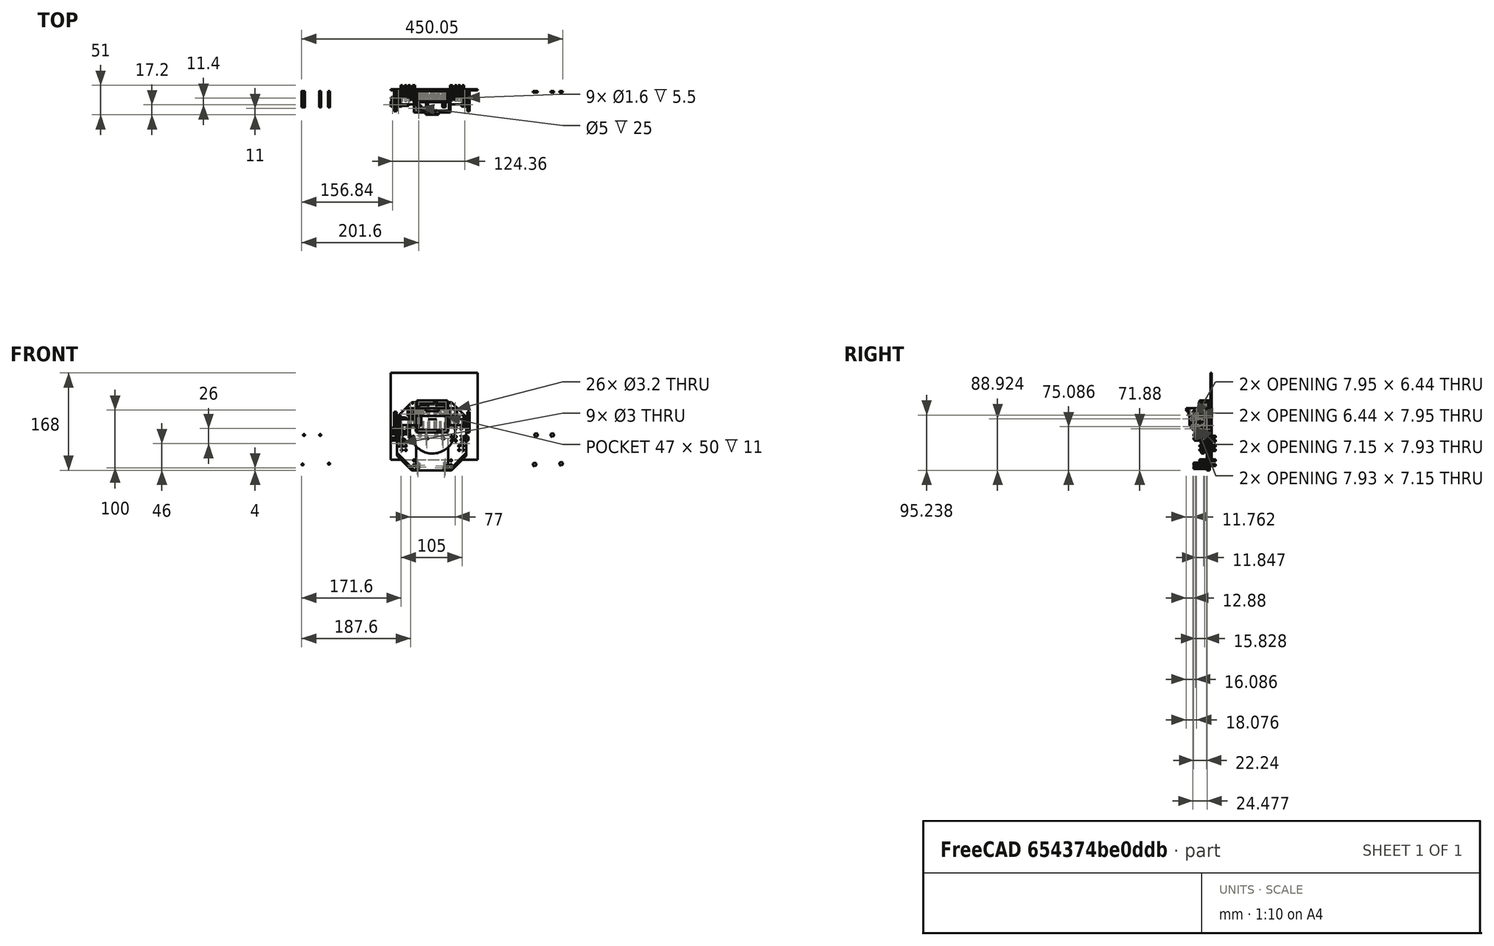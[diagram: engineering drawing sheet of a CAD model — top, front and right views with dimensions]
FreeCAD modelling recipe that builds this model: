
FCSTD DOCUMENT  (FreeCAD 0.17R13522 (Git))
Label: 5028.7 Frank
License: All rights reserved
LicenseURL: http://en.wikipedia.org/wiki/All_rights_reserved
objects: Part::Cylinder×138, Part::Box×78, Part::Cut×74, Part::Fuse×72, Part::MultiFuse×39, Part::Feature×37, Part::Chamfer×23, Part::Fillet×19, Part::Mirroring×15, Part::Cone×9, Part::Compound×3, Part::Torus×2, App::DocumentObjectGroup×1
note: 509 computed .brp shape members not serialized (recipe doc carries the construction recipe); baked Part::Feature solids carry a one-line shape summary decoded from their .brp

FEATURE [Part::Cylinder] Cylinder
  Angle = 360
  AttacherType = Attacher::AttachEngine3D
  Height = 30
  Radius = 7
FEATURE [Part::Cylinder] Cylinder001
  Angle = 360
  AttacherType = Attacher::AttachEngine3D
  Height = 19
  Placement = pos=(0,0,30) rot=(0,0,1;0rad)
  Radius = 7
FEATURE [Part::Cylinder] Cylinder002
  Angle = 360
  AttacherType = Attacher::AttachEngine3D
  Height = 1.8
  Placement = pos=(0,0,49) rot=(0,0,1;0rad)
  Radius = 2.5
FEATURE [Part::Compound] Compound
  Links = -> [Cylinder,Cylinder002,Cylinder001]
FEATURE [Part::Cylinder] Cylinder003
  Angle = 360
  AttacherType = Attacher::AttachEngine3D
  Height = 30
  Radius = 7
FEATURE [Part::Cylinder] Cylinder004
  Angle = 360
  AttacherType = Attacher::AttachEngine3D
  Height = 19
  Placement = pos=(0,0,30) rot=(0,0,1;0rad)
  Radius = 7
FEATURE [Part::Cylinder] Cylinder005
  Angle = 360
  AttacherType = Attacher::AttachEngine3D
  Height = 1.8
  Placement = pos=(0,0,49) rot=(0,0,1;0rad)
  Radius = 2.5
FEATURE [Part::Compound] Compound001
  Links = -> [Cylinder003,Cylinder005,Cylinder004]
  Placement = pos=(14.5,0,50) rot=(1,0,0;3.14159rad)
FEATURE [Part::Cylinder] Cylinder006
  Angle = 360
  AttacherType = Attacher::AttachEngine3D
  Height = 30
  Radius = 7
FEATURE [Part::Cylinder] Cylinder007
  Angle = 360
  AttacherType = Attacher::AttachEngine3D
  Height = 19
  Placement = pos=(0,0,30) rot=(0,0,1;0rad)
  Radius = 7
FEATURE [Part::Cylinder] Cylinder008
  Angle = 360
  AttacherType = Attacher::AttachEngine3D
  Height = 1.8
  Placement = pos=(0,0,49) rot=(0,0,1;0rad)
  Radius = 2.5
FEATURE [Part::Compound] Compound002
  Links = -> [Cylinder006,Cylinder008,Cylinder007]
  Placement = pos=(29,0,0) rot=(0,0,1;0rad)
FEATURE [Part::Box] Box  label="Cube"
  AttacherType = Attacher::AttachEngine3D
  Height = 50
  Length = 47
  Placement = pos=(-9,-8,0) rot=(0,0,1;0rad)
  Width = 12
FEATURE [Part::Box] Box001  label="Cube001"
  AttacherType = Attacher::AttachEngine3D
  Height = 55
  Length = 53
  Placement = pos=(-12,-8,-2.5) rot=(0,0,1;0rad)
  Width = 11
FEATURE [Part::Cylinder] Cylinder009
  Angle = 360
  AttacherType = Attacher::AttachEngine3D
  Height = 50
  Radius = 7
FEATURE [Part::Cylinder] Cylinder010
  Angle = 360
  AttacherType = Attacher::AttachEngine3D
  Height = 50
  Placement = pos=(14.5,0,0) rot=(0,0,1;0rad)
  Radius = 7
FEATURE [Part::Cut] Cut
  Base = -> Box001
  Tool = -> Box
FEATURE [Part::Box] Box002  label="Cube002"
  AttacherType = Attacher::AttachEngine3D
  Height = 55
  Length = 53
  Placement = pos=(-12,3,-2.5) rot=(0,0,1;0rad)
  Width = 7
FEATURE [Part::Fuse] Fusion
  Base = -> Cut
  Tool = -> Box002
FEATURE [Part::Cut] Cut001  label="No idea why this is here...."
  Base = -> Fusion
  Tool = -> Cylinder009
FEATURE [Part::Cylinder] Cylinder011
  Angle = 360
  AttacherType = Attacher::AttachEngine3D
  Height = 50
  Placement = pos=(29,0,0) rot=(0,0,1;0rad)
  Radius = 7
FEATURE [Part::Box] Box003  label="Cube003"
  AttacherType = Attacher::AttachEngine3D
  Height = 5
  Length = 2
  Placement = pos=(28,-9,-2) rot=(0,0,1;0rad)
  Width = 12
FEATURE [Part::Box] Box004  label="Cube004"
  AttacherType = Attacher::AttachEngine3D
  Height = 5
  Length = 2
  Placement = pos=(18.5,-9,46) rot=(0,0,1;0rad)
  Width = 12
FEATURE [Part::Box] Box005  label="Cube005"
  AttacherType = Attacher::AttachEngine3D
  Height = 5
  Length = 2
  Placement = pos=(-2,-9,46) rot=(0,0,1;0rad)
  Width = 12
FEATURE [Part::Box] Box006  label="Cube006"
  AttacherType = Attacher::AttachEngine3D
  Height = 5
  Length = 3
  Placement = pos=(35,-9,-4) rot=(0,0,1;0rad)
  Width = 12
FEATURE [Part::Cut] Cut008
FEATURE [Part::Torus] Torus001
  Angle1 = -180
  Angle2 = 180
  Angle3 = 360
  AttacherType = Attacher::AttachEngine3D
  Placement = pos=(0,0,2) rot=(0,0,1;0rad)
  Radius1 = 19
  Radius2 = 1.5
FEATURE [Part::Cut] Cut009  label="wheel2"
  Base = -> Cut008
  Placement = pos=(75,-7,15) rot=(0,1,0;1.5708rad)
  Tool = -> Torus001
FEATURE [Part::Torus] Torus
  Angle1 = -180
  Angle2 = 180
  Angle3 = 360
  AttacherType = Attacher::AttachEngine3D
  Placement = pos=(0,0,2) rot=(0,0,1;0rad)
  Radius1 = 19
  Radius2 = 1.5
FEATURE [Part::Cut] Cut010
FEATURE [Part::Cut] Cut011  label="wheel1"
  Base = -> Cut010
  Placement = pos=(-51,-7,15) rot=(0,1,0;1.5708rad)
  Tool = -> Torus
FEATURE [Part::Fuse] Fusion003
FEATURE [Part::Cylinder] Cylinder012
  Angle = 360
  AttacherType = Attacher::AttachEngine3D
  Height = 10
  Placement = pos=(5,-4.5,0) rot=(0,1,0;1.5708rad)
  Radius = 0.8
FEATURE [Part::Fuse] Fusion048  label="right-motor001"
  Base = -> Cylinder012
  Placement = pos=(-51,-7,15) rot=(0,0,1;0rad)
  Tool = -> Fusion003
FEATURE [Part::Fuse] Fusion049
FEATURE [Part::Cylinder] Cylinder013
  Angle = 360
  AttacherType = Attacher::AttachEngine3D
  Height = 10
  Placement = pos=(5,-4.5,0) rot=(0,1,0;1.5708rad)
  Radius = 0.8
FEATURE [Part::Fuse] Fusion050  label="left-motor001"
  Base = -> Cylinder013
  Placement = pos=(79,-7,15) rot=(0,0,1;3.14159rad)
  Tool = -> Fusion049
FEATURE [Part::Box] Box007  label="Cube007"
  AttacherType = Attacher::AttachEngine3D
  Height = 5
  Length = 2
  Placement = pos=(37.5,-9,46) rot=(0,0,1;0rad)
  Width = 12
FEATURE [Part::Box] Box008  label="Cube008"
  AttacherType = Attacher::AttachEngine3D
  Height = 5
  Length = 2
  Placement = pos=(8,-9,-2) rot=(0,0,1;0rad)
  Width = 12
FEATURE [Part::Box] Box009  label="The Ground"
  AttacherType = Attacher::AttachEngine3D
  Height = 150
  Length = 150
  Placement = pos=(-57,11,-50) rot=(0,0,1;0rad)
  Width = 2
FEATURE [Part::Box] Box010  label="Motor Mount Left"
  AttacherType = Attacher::AttachEngine3D
  Height = 16
  Length = 4
  Placement = pos=(69,-13,7) rot=(0,0,1;0rad)
  Width = 20
FEATURE [Part::Box] Box011  label="Motor Mount Right"
  AttacherType = Attacher::AttachEngine3D
  Height = 16
  Length = 4
  Placement = pos=(-46,-13,7) rot=(0,0,1;0rad)
  Width = 20
FEATURE [Part::Box] Box012  label="Motor Support Right"
  AttacherType = Attacher::AttachEngine3D
  Height = 16
  Length = 10
  Placement = pos=(-25,-1,7) rot=(0,0,1;0rad)
  Width = 8
FEATURE [Part::Box] Box013  label="Motor Support Left"
  AttacherType = Attacher::AttachEngine3D
  Height = 16
  Length = 10
  Placement = pos=(43,-1,7) rot=(0,0,1;0rad)
  Width = 8
FEATURE [Part::Cylinder] Cylinder014
  Angle = 360
  AttacherType = Attacher::AttachEngine3D
  Height = 28
  Placement = pos=(40.7,0,-10.3) rot=(1,0,0;1.5708rad)
  Radius = 1.6
FEATURE [Part::Cylinder] Cylinder015
  Angle = 360
  AttacherType = Attacher::AttachEngine3D
  Height = 28
  Placement = pos=(-2.4,0,-59.8) rot=(1,0,0;1.5708rad)
  Radius = 1.6
FEATURE [Part::Cylinder] Cylinder016
  Angle = 360
  AttacherType = Attacher::AttachEngine3D
  Height = 28
  Placement = pos=(-5,0,-9) rot=(1,0,0;1.5708rad)
  Radius = 1.6
FEATURE [Part::Cylinder] Cylinder017
  Angle = 360
  AttacherType = Attacher::AttachEngine3D
  Height = 28
  Placement = pos=(25.5,0,-59.8) rot=(1,0,0;1.5708rad)
  Radius = 1.6
FEATURE [Part::Fuse] Fusion051
  Base = -> Cylinder015
  Tool = -> Cylinder016
FEATURE [Part::Fuse] Fusion052
  Base = -> Cylinder014
  Tool = -> Cylinder017
FEATURE [Part::Fuse] Fusion053  label="Screw holes on Arduino Duo"
  Base = -> Fusion051
  Tool = -> Fusion052
FEATURE [Part::Mirroring] Part__Mirroring  label="XXXXXScrew holes on Arduino Duo (Mirror #1)"
  Base = (0,0,0)
  Normal = (0,0,1)
  Placement = pos=(-204,10,-67) rot=(0,0,1;0rad)
  Source = -> Fusion053
FEATURE [Part::Box] Box014  label="Not used Cube"
  AttacherType = Attacher::AttachEngine3D
  Height = 10
  Length = 10
  Placement = pos=(-1,4,-5.85) rot=(0,0,1;0rad)
  Width = 10
FEATURE [Part::Box] Box015  label="Cube014 Arduino Support cube"
  AttacherType = Attacher::AttachEngine3D
  Height = 67
  Length = 55
  Placement = pos=(-13,5,-68) rot=(0,0,1;0rad)
  Width = 5
FEATURE [Part::Cylinder] Cylinder018
  Angle = 360
  AttacherType = Attacher::AttachEngine3D
  Height = 5
  Placement = pos=(15,0,0) rot=(1,0,0;1.5708rad)
  Radius = 39
FEATURE [Part::Cut] Cut014  label="M3 Nut"
  Base = -> Cut001
  Placement = pos=(-6.4,10,-7.2) rot=(1,0,0;1.5708rad)
  Tool = -> Cylinder001
FEATURE [Part::Cut] Cut015  label="M3 Nut001"
  Base = -> Cut001
  Placement = pos=(21.5,10,-7.2) rot=(1,0,0;1.5708rad)
  Tool = -> Cylinder001
FEATURE [Part::Cut] Cut016  label="M3 Nut002"
  Base = -> Cut001
  Placement = pos=(36.7,10,-56.7) rot=(1,0,0;1.5708rad)
  Tool = -> Cylinder001
FEATURE [Part::Cut] Cut017  label="M3 Nut003"
  Base = -> Cut001
  Placement = pos=(-9,10,-58) rot=(1,0,0;1.5708rad)
  Tool = -> Cylinder001
FEATURE [Part::Cut] Cut018
  Base = -> Cut
  Placement = pos=(-9,10,-58) rot=(1,0,0;1.5708rad)
  Tool = -> Box006
FEATURE [Part::Cut] Cut019
  Base = -> Cut
  Placement = pos=(36.7,10,-56.7) rot=(1,0,0;1.5708rad)
  Tool = -> Box006
FEATURE [Part::Cut] Cut020
  Base = -> Cut
  Placement = pos=(-6.4,10,-7.2) rot=(1,0,0;1.5708rad)
  Tool = -> Box006
FEATURE [Part::Cut] Cut021
  Base = -> Cut
  Placement = pos=(21.5,10,-7.2) rot=(1,0,0;1.5708rad)
  Tool = -> Box006
FEATURE [Part::MultiFuse] Fusion054  label="XXXXXHex Holes"
  Placement = pos=(200,0,0) rot=(0,0,1;0rad)
  Shapes = -> [Cut018,Cut021,Cut019,Cut020]
FEATURE [Part::Box] Box016  label="Cube015"
  AttacherType = Attacher::AttachEngine3D
  Height = 117
  Length = 33
  Placement = pos=(-46,7,-68) rot=(0,0,1;0rad)
  Width = 3
FEATURE [Part::Box] Box017  label="Cube016"
  AttacherType = Attacher::AttachEngine3D
  Height = 117
  Length = 31
  Placement = pos=(42,7,-68) rot=(0,0,1;0rad)
  Width = 3
FEATURE [Part::Cylinder] Cylinder019
  Angle = 360
  AttacherType = Attacher::AttachEngine3D
  Height = 28
  Placement = pos=(48,20,-10) rot=(1,0,0;1.5708rad)
  Radius = 1.6
FEATURE [Part::Cylinder] Cylinder020
  Angle = 360
  AttacherType = Attacher::AttachEngine3D
  Height = 28
  Placement = pos=(47,20,-51) rot=(1,0,0;1.5708rad)
  Radius = 1.6
FEATURE [Part::Cylinder] Cylinder021
  Angle = 360
  AttacherType = Attacher::AttachEngine3D
  Height = 28
  Placement = pos=(48,20,-17) rot=(1,0,0;1.5708rad)
  Radius = 1.6
FEATURE [Part::Cylinder] Cylinder022
  Angle = 360
  AttacherType = Attacher::AttachEngine3D
  Height = 28
  Placement = pos=(47,20,-59) rot=(1,0,0;1.5708rad)
  Radius = 1.6
FEATURE [Part::Cylinder] Cylinder023
  Angle = 360
  AttacherType = Attacher::AttachEngine3D
  Height = 28
  Placement = pos=(55,20,-17) rot=(1,0,0;1.5708rad)
  Radius = 1.6
FEATURE [Part::Cylinder] Cylinder024
  Angle = 360
  AttacherType = Attacher::AttachEngine3D
  Height = 28
  Placement = pos=(55,20,-10) rot=(1,0,0;1.5708rad)
  Radius = 1.6
FEATURE [Part::MultiFuse] Fusion055
  Shapes = -> [Cylinder021,Cylinder023,Cylinder024,Cylinder019]
FEATURE [Part::MultiFuse] Fusion056
  Placement = pos=(13,0,-16) rot=(0,0,1;0rad)
  Shapes = -> [Cylinder021,Cylinder023,Cylinder024,Cylinder019]
FEATURE [Part::MultiFuse] Fusion057  label="Mount holes top left"
  Placement = pos=(-1,0,46) rot=(0,0,1;0rad)
  Shapes = -> [Cylinder021,Cylinder023,Cylinder024,Cylinder019]
FEATURE [Part::MultiFuse] Fusion058  label="Mount holes top right"
  Placement = pos=(-71,0,46) rot=(0,0,1;0rad)
  Shapes = -> [Cylinder021,Cylinder023,Cylinder024,Cylinder019]
FEATURE [Part::MultiFuse] Fusion059
  Shapes = -> [Cylinder022,Cylinder020,Fusion055,Fusion056]
FEATURE [Part::Mirroring] Part__Mirroring001  label="Mount holes bottom right"
  Base = (0,0,0)
  Normal = (1,0,0)
  Placement = pos=(30,0,0) rot=(0,0,1;0rad)
  Source = -> Fusion059
FEATURE [Part::Cylinder] Cylinder025
  Angle = 360
  AttacherType = Attacher::AttachEngine3D
  Height = 28
  Placement = pos=(48,20,-10) rot=(1,0,0;1.5708rad)
  Radius = 1.6
FEATURE [Part::Cylinder] Cylinder026
  Angle = 360
  AttacherType = Attacher::AttachEngine3D
  Height = 28
  Placement = pos=(47,20,-51) rot=(1,0,0;1.5708rad)
  Radius = 1.6
FEATURE [Part::Cylinder] Cylinder027
  Angle = 360
  AttacherType = Attacher::AttachEngine3D
  Height = 28
  Placement = pos=(48,20,-17) rot=(1,0,0;1.5708rad)
  Radius = 1.6
FEATURE [Part::Cylinder] Cylinder028
  Angle = 360
  AttacherType = Attacher::AttachEngine3D
  Height = 28
  Placement = pos=(47,20,-59) rot=(1,0,0;1.5708rad)
  Radius = 1.6
FEATURE [Part::Cylinder] Cylinder029
  Angle = 360
  AttacherType = Attacher::AttachEngine3D
  Height = 28
  Placement = pos=(55,20,-17) rot=(1,0,0;1.5708rad)
  Radius = 1.6
FEATURE [Part::Cylinder] Cylinder030
  Angle = 360
  AttacherType = Attacher::AttachEngine3D
  Height = 28
  Placement = pos=(55,20,-10) rot=(1,0,0;1.5708rad)
  Radius = 1.6
FEATURE [Part::MultiFuse] Fusion060
  Shapes = -> [Cylinder027,Cylinder029,Cylinder030,Cylinder025]
FEATURE [Part::MultiFuse] Fusion061
  Placement = pos=(13,0,-16) rot=(0,0,1;0rad)
  Shapes = -> [Cylinder027,Cylinder029,Cylinder030,Cylinder025]
FEATURE [Part::MultiFuse] Fusion062  label="Mount holes bottom left"
  Shapes = -> [Cylinder028,Cylinder026,Fusion060,Fusion061]
FEATURE [Part::Cylinder] Cylinder031  label="Cylinder127"
  Angle = 360
  AttacherType = Attacher::AttachEngine3D
  Height = 10
  Placement = pos=(0,18,29) rot=(0,0,1;0rad)
  Radius = 2.25
FEATURE [Part::Cylinder] Cylinder032  label="Cylinder128"
  Angle = 360
  AttacherType = Attacher::AttachEngine3D
  Height = 10
  Placement = pos=(4.5,18,32) rot=(0,0,1;0rad)
  Radius = 1
FEATURE [Part::Cylinder] Cylinder033  label="Cylinder129"
  Angle = 360
  AttacherType = Attacher::AttachEngine3D
  Height = 10
  Placement = pos=(-4.5,18,32) rot=(0,0,1;0rad)
  Radius = 1
FEATURE [Part::Fuse] Fusion009  label="Mounting Screw Holes"
  Base = -> Cylinder032
  Tool = -> Cylinder033
FEATURE [Part::Fuse] Fusion071  label="Motor Holes Left"
  Base = -> Cylinder031
  Placement = pos=(37,-7,-3) rot=(0.57735,0.57735,0.57735;2.0944rad)
  Tool = -> Fusion009
FEATURE [Part::Cylinder] Cylinder034  label="Cylinder130"
  Angle = 360
  AttacherType = Attacher::AttachEngine3D
  Height = 10
  Placement = pos=(0,18,29) rot=(0,0,1;0rad)
  Radius = 2.25
FEATURE [Part::Cylinder] Cylinder035  label="Cylinder131"
  Angle = 360
  AttacherType = Attacher::AttachEngine3D
  Height = 10
  Placement = pos=(4.5,18,32) rot=(0,0,1;0rad)
  Radius = 1
FEATURE [Part::Cylinder] Cylinder036  label="Cylinder132"
  Angle = 360
  AttacherType = Attacher::AttachEngine3D
  Height = 10
  Placement = pos=(-4.5,18,32) rot=(0,0,1;0rad)
  Radius = 1
FEATURE [Part::Fuse] Fusion072  label="Mounting Screw Holes001"
  Base = -> Cylinder035
  Tool = -> Cylinder036
FEATURE [Part::Fuse] Fusion073  label="Motor Holes Right"
  Base = -> Cylinder034
  Placement = pos=(-79,-7,-3) rot=(0.57735,0.57735,0.57735;2.0944rad)
  Tool = -> Fusion072
FEATURE [Part::Cylinder] Cylinder037  label="Cylinder133"
  Angle = 360
  AttacherType = Attacher::AttachEngine3D
  Height = 28
  Placement = pos=(40.7,0,-10.3) rot=(1,0,0;1.5708rad)
  Radius = 1.6
FEATURE [Part::Cylinder] Cylinder038  label="Cylinder134"
  Angle = 360
  AttacherType = Attacher::AttachEngine3D
  Height = 28
  Placement = pos=(-2.4,0,-59.8) rot=(1,0,0;1.5708rad)
  Radius = 1.6
FEATURE [Part::Cylinder] Cylinder039  label="Cylinder135"
  Angle = 360
  AttacherType = Attacher::AttachEngine3D
  Height = 28
  Placement = pos=(-5,0,-9) rot=(1,0,0;1.5708rad)
  Radius = 1.6
FEATURE [Part::Cylinder] Cylinder040  label="Cylinder136"
  Angle = 360
  AttacherType = Attacher::AttachEngine3D
  Height = 28
  Placement = pos=(25.5,0,-59.8) rot=(1,0,0;1.5708rad)
  Radius = 1.6
FEATURE [Part::Fuse] Fusion074
  Base = -> Cylinder038
  Tool = -> Cylinder039
FEATURE [Part::Fuse] Fusion075
  Base = -> Cylinder037
  Tool = -> Cylinder040
FEATURE [Part::Fuse] Fusion076  label="Screw holes on Arduino Duo001"
  Base = -> Fusion074
  Tool = -> Fusion075
FEATURE [Part::Mirroring] Part__Mirroring002  label="Screw holes on Arduino Duo (Mirror #1)001"
  Base = (0,0,0)
  Normal = (0,0,1)
  Placement = pos=(-4,10,-67) rot=(0,0,1;0rad)
  Source = -> Fusion076
FEATURE [Part::Mirroring] Part__Mirroring003  label="Screw holes on Arduino Duo (Mirror #1)001 (Mirror #4)"
  Base = (0,0,0)
  Normal = (1,0,0)
  Placement = pos=(27,0,-6) rot=(0,0,1;0rad)
  Source = -> Part__Mirroring002
FEATURE [Part::Box] Box018  label="Cube017"
  AttacherType = Attacher::AttachEngine3D
  Height = 50
  Length = 47
  Placement = pos=(-9,-8,0) rot=(0,0,1;0rad)
  Width = 12
FEATURE [Part::Box] Box019  label="Cube018"
  AttacherType = Attacher::AttachEngine3D
  Height = 55
  Length = 53
  Placement = pos=(-12,-8,-2.5) rot=(0,0,1;0rad)
  Width = 11
FEATURE [Part::Cut] Cut031
  Base = -> Box019
  Tool = -> Box018
FEATURE [Part::Box] Box020  label="Cube019"
  AttacherType = Attacher::AttachEngine3D
  Height = 5
  Length = 3
  Placement = pos=(35,-9,-4) rot=(0,0,1;0rad)
  Width = 12
FEATURE [Part::Cut] Cut032
  Base = -> Cut031
  Placement = pos=(-9,10,-58) rot=(1,0,0;1.5708rad)
  Tool = -> Box020
FEATURE [Part::Cut] Cut033
  Base = -> Cut031
  Placement = pos=(36.7,10,-56.7) rot=(1,0,0;1.5708rad)
  Tool = -> Box020
FEATURE [Part::Cut] Cut034
  Base = -> Cut031
  Placement = pos=(-6.4,10,-7.2) rot=(1,0,0;1.5708rad)
  Tool = -> Box020
FEATURE [Part::Cut] Cut035
  Base = -> Cut031
  Placement = pos=(21.5,10,-7.2) rot=(1,0,0;1.5708rad)
  Tool = -> Box020
FEATURE [Part::MultiFuse] Fusion077
  Shapes = -> [Cut032,Cut035,Cut033,Cut034]
FEATURE [Part::Mirroring] Part__Mirroring004  label="Hex Holes"
  Base = (0,0,0)
  Normal = (1,0,0)
  Placement = pos=(27,0,-6) rot=(0,0,1;0rad)
  Source = -> Fusion077
FEATURE [Part::Box] Box021  label="Cube020"
  AttacherType = Attacher::AttachEngine3D
  Height = 13
  Length = 63
  Placement = pos=(-17,-27,26) rot=(0,0,1;0rad)
  Width = 34
FEATURE [Part::Box] Box022  label="Cube021"
  AttacherType = Attacher::AttachEngine3D
  Height = 13
  Length = 12
  Placement = pos=(45,4,26) rot=(0,0,1;0rad)
  Width = 3
FEATURE [Part::Box] Box023  label="Cube022"
  AttacherType = Attacher::AttachEngine3D
  Height = 13
  Length = 12
  Placement = pos=(-28,4,26) rot=(0,0,1;0rad)
  Width = 3
FEATURE [Part::Box] Box024  label="Cube023"
  AttacherType = Attacher::AttachEngine3D
  Height = 13
  Length = 57
  Placement = pos=(-14,-24,26) rot=(0,0,1;0rad)
  Width = 31
FEATURE [Part::Cylinder] Cylinder041  label="Cylinder137"
  Angle = 360
  AttacherType = Attacher::AttachEngine3D
  Height = 28
  Placement = pos=(54,20,29) rot=(1,0,0;1.5708rad)
  Radius = 1.6
FEATURE [Part::Cylinder] Cylinder042  label="Cylinder138"
  Angle = 360
  AttacherType = Attacher::AttachEngine3D
  Height = 28
  Placement = pos=(54,20,36) rot=(1,0,0;1.5708rad)
  Radius = 1.6
FEATURE [Part::Cylinder] Cylinder043  label="Cylinder139"
  Angle = 360
  AttacherType = Attacher::AttachEngine3D
  Height = 28
  Placement = pos=(-23,20,29) rot=(1,0,0;1.5708rad)
  Radius = 1.6
FEATURE [Part::Cylinder] Cylinder044  label="Cylinder140"
  Angle = 360
  AttacherType = Attacher::AttachEngine3D
  Height = 28
  Placement = pos=(-23,20,36) rot=(1,0,0;1.5708rad)
  Radius = 1.6
FEATURE [Part::Cylinder] Cylinder045  label="Cylinder141"
  Angle = 360
  AttacherType = Attacher::AttachEngine3D
  Height = 10
  Placement = pos=(36,-17.25,32.5) rot=(0,1,0;1.5708rad)
  Radius = 2.5
FEATURE [Part::Cut] Cut037
  Base = -> Box021
  Tool = -> Box024
FEATURE [Part::Cut] Cut038
  Base = -> Cut037
  Tool = -> Cylinder045
FEATURE [Part::Box] Box025  label="Cube024"
  AttacherType = Attacher::AttachEngine3D
  Height = 5
  Length = 22
  Placement = pos=(3.5,-31,34) rot=(0,0,1;0rad)
  Width = 4
FEATURE [Part::Cylinder] Cylinder046  label="Cylinder142"
  Angle = 360
  AttacherType = Attacher::AttachEngine3D
  Height = 10
  Placement = pos=(20.75,-29,30) rot=(0,0,1;0rad)
  Radius = 0.85
FEATURE [Part::Cylinder] Cylinder047  label="Cylinder143"
  Angle = 360
  AttacherType = Attacher::AttachEngine3D
  Height = 10
  Placement = pos=(8.25,-29,40) rot=(1,0,0;3.14159rad)
  Radius = 0.85
FEATURE [Part::Fuse] Fusion078
  Base = -> Cylinder046
  Tool = -> Cylinder047
FEATURE [Part::Cut] Cut039
  Base = -> Box025
  Tool = -> Fusion078
FEATURE [Part::Fuse] Fusion079
  Base = -> Cut038
  Tool = -> Cut039
FEATURE [Part::Fuse] Fusion080
  Base = -> Cylinder043
  Tool = -> Cylinder044
FEATURE [Part::Fuse] Fusion081
  Base = -> Cylinder041
  Tool = -> Cylinder042
FEATURE [Part::Fuse] Fusion082
  Base = -> Box023
  Tool = -> Fusion079
FEATURE [Part::Fuse] Fusion083
  Base = -> Box022
  Tool = -> Fusion082
FEATURE [Part::Cut] Cut040
  Base = -> Fusion083
  Tool = -> Fusion081
FEATURE [Part::Cut] Cut041  label="Switch Bracket"
  Base = -> Cut040
  Tool = -> Fusion080
FEATURE [Part::Cylinder] Cylinder048  label="Cylinder144"
  Angle = 360
  AttacherType = Attacher::AttachEngine3D
  Height = 28
  Placement = pos=(-23,20,29) rot=(1,0,0;1.5708rad)
  Radius = 1.6
FEATURE [Part::Cylinder] Cylinder049  label="Cylinder145"
  Angle = 360
  AttacherType = Attacher::AttachEngine3D
  Height = 28
  Placement = pos=(-23,20,36) rot=(1,0,0;1.5708rad)
  Radius = 1.6
FEATURE [Part::Fuse] Fusion084
  Base = -> Cylinder048
  Placement = pos=(1,0,0) rot=(0,0,1;0rad)
  Tool = -> Cylinder049
FEATURE [Part::Cylinder] Cylinder050  label="Cylinder146"
  Angle = 360
  AttacherType = Attacher::AttachEngine3D
  Height = 28
  Placement = pos=(-23,20,29) rot=(1,0,0;1.5708rad)
  Radius = 1.6
FEATURE [Part::Cylinder] Cylinder051  label="Cylinder147"
  Angle = 360
  AttacherType = Attacher::AttachEngine3D
  Height = 28
  Placement = pos=(-23,20,36) rot=(1,0,0;1.5708rad)
  Radius = 1.6
FEATURE [Part::Fuse] Fusion085
  Base = -> Cylinder050
  Placement = pos=(-1,0,0) rot=(0,0,1;0rad)
  Tool = -> Cylinder051
FEATURE [Part::Cut] Cut042
  Base = -> Cut041
  Tool = -> Fusion084
FEATURE [Part::Cut] Cut043  label="Switch Bracket001"
  Base = -> Cut042
  Tool = -> Fusion085
FEATURE [Part::Cylinder] Cylinder052  label="Cylinder148"
  Angle = 360
  AttacherType = Attacher::AttachEngine3D
  Height = 42
  Radius = 5.15
FEATURE [Part::Cylinder] Cylinder053  label="Cylinder149"
  Angle = 360
  AttacherType = Attacher::AttachEngine3D
  Height = 1.6
  Placement = pos=(0,0,42) rot=(0,0,1;0rad)
  Radius = 1.65
FEATURE [Part::Fuse] Fusion086
  Base = -> Cylinder052
  Placement = pos=(2,0,0) rot=(0,0,1;0rad)
  Tool = -> Cylinder053
FEATURE [Part::Cylinder] Cylinder054  label="Cylinder150"
  Angle = 360
  AttacherType = Attacher::AttachEngine3D
  Height = 42
  Radius = 4.8
FEATURE [Part::Cylinder] Cylinder055  label="Cylinder151"
  Angle = 360
  AttacherType = Attacher::AttachEngine3D
  Height = 1.6
  Placement = pos=(0,0,42) rot=(0,0,1;0rad)
  Radius = 1.65
FEATURE [Part::Fuse] Fusion087
  Base = -> Cylinder054
  Placement = pos=(12,0,0) rot=(0,0,1;0rad)
  Tool = -> Cylinder055
FEATURE [Part::Cylinder] Cylinder056  label="Cylinder152"
  Angle = 360
  AttacherType = Attacher::AttachEngine3D
  Height = 42
  Radius = 4.8
FEATURE [Part::Cylinder] Cylinder057  label="Cylinder153"
  Angle = 360
  AttacherType = Attacher::AttachEngine3D
  Height = 1.6
  Placement = pos=(0,0,42) rot=(0,0,1;0rad)
  Radius = 1.65
FEATURE [Part::Fuse] Fusion088
  Base = -> Cylinder056
  Placement = pos=(22,0,0) rot=(0,0,1;0rad)
  Tool = -> Cylinder057
FEATURE [Part::Cylinder] Cylinder058  label="Cylinder154"
  Angle = 360
  AttacherType = Attacher::AttachEngine3D
  Height = 42
  Radius = 4.8
FEATURE [Part::Cylinder] Cylinder059  label="Cylinder155"
  Angle = 360
  AttacherType = Attacher::AttachEngine3D
  Height = 1.6
  Placement = pos=(0,0,42) rot=(0,0,1;0rad)
  Radius = 1.65
FEATURE [Part::Fuse] Fusion089
  Base = -> Cylinder058
  Placement = pos=(32,0,0) rot=(0,0,1;0rad)
  Tool = -> Cylinder059
FEATURE [Part::Cylinder] Cylinder060  label="Cylinder156"
  Angle = 360
  AttacherType = Attacher::AttachEngine3D
  Height = 42
  Radius = 5.15
FEATURE [Part::Cylinder] Cylinder061  label="Cylinder157"
  Angle = 360
  AttacherType = Attacher::AttachEngine3D
  Height = 1.6
  Placement = pos=(0,0,42) rot=(0,0,1;0rad)
  Radius = 1.65
FEATURE [Part::Fuse] Fusion093
  Base = -> Cylinder060
  Placement = pos=(-8,0,0) rot=(0,0,1;0rad)
  Tool = -> Cylinder061
FEATURE [Part::MultiFuse] Fusion094  label="AAA Batts"
  Placement = pos=(2.5,0,2) rot=(0,0,1;0rad)
  Shapes = -> [Fusion093,Fusion086,Fusion087,Fusion088,Fusion089]
FEATURE [Part::Cylinder] Cylinder062  label="Cylinder158"
  Angle = 360
  AttacherType = Attacher::AttachEngine3D
  Height = 10
  Radius = 17
FEATURE [Part::Cylinder] Cylinder063  label="Cylinder159"
  Angle = 360
  AttacherType = Attacher::AttachEngine3D
  Height = 16
  Placement = pos=(0,0,-4) rot=(0,0,1;0rad)
  Radius = 10
FEATURE [Part::Cut] Cut044
  Base = -> Cylinder062
  Tool = -> Cylinder063
FEATURE [Part::Box] Box026  label="Cube025"
  AttacherType = Attacher::AttachEngine3D
  Height = 20
  Length = 18
  Placement = pos=(0,0,-5) rot=(0,0,1;0rad)
  Width = 20
FEATURE [Part::Box] Box027  label="Cube026"
  AttacherType = Attacher::AttachEngine3D
  Height = 20
  Length = 10
  Placement = pos=(0,0,-5) rot=(0,0,1;0.174533rad)
  Width = 20
FEATURE [Part::Cut] Cut045
  Base = -> Box027
  Tool = -> Box026
FEATURE [Part::Feature] Cut045001
  Placement = pos=(0,0,0) rot=(0,0,1;0.349066rad)
  shape: bbox 10 x 22.32 x 20 mm, 7 faces (baked)
FEATURE [Part::Feature] Cut045002
  Placement = pos=(0,0,0) rot=(0,0,1;0.698132rad)
  shape: bbox 15.32 x 20.52 x 20 mm, 7 faces (baked)
FEATURE [Part::Feature] Cut045003
  Placement = pos=(0,0,0) rot=(0,0,1;1.0472rad)
  shape: bbox 18.79 x 16.24 x 20 mm, 7 faces (baked)
FEATURE [Part::Feature] Cut045004
  Placement = pos=(0,0,0) rot=(0,0,1;1.39626rad)
  shape: bbox 20 x 10 x 20 mm, 7 faces (baked)
FEATURE [Part::Feature] Cut045005
  Placement = pos=(0,0,0) rot=(0,0,1;1.74533rad)
  shape: bbox 22.21 x 9.894 x 20 mm, 7 faces (baked)
FEATURE [Part::Feature] Cut045006
  Placement = pos=(0,0,0) rot=(0,0,1;2.0944rad)
  shape: bbox 21.75 x 12.86 x 20 mm, 7 faces (baked)
FEATURE [Part::Feature] Cut045007
  Placement = pos=(0,0,0) rot=(0,0,1;2.44346rad)
  shape: bbox 18.66 x 17.32 x 20 mm, 7 faces (baked)
FEATURE [Part::Feature] Cut045008
  Placement = pos=(0,0,0) rot=(0,0,1;2.79253rad)
  shape: bbox 13.32 x 19.7 x 20 mm, 7 faces (baked)
FEATURE [Part::Feature] Cut045009
  Placement = pos=(0,0,0) rot=(0,0,1;3.14159rad)
  shape: bbox 10.1 x 21.43 x 20 mm, 7 faces (baked)
FEATURE [Part::Feature] Cut045010
  Placement = pos=(0,0,0) rot=(0,0,1;3.49066rad)
  shape: bbox 10 x 22.32 x 20 mm, 7 faces (baked)
FEATURE [Part::Feature] Cut045011
  Placement = pos=(0,0,0) rot=(0,0,1;3.83972rad)
  shape: bbox 15.32 x 20.52 x 20 mm, 7 faces (baked)
FEATURE [Part::Feature] Cut045012
  Placement = pos=(0,0,0) rot=(0,0,1;4.18879rad)
  shape: bbox 18.79 x 16.24 x 20 mm, 7 faces (baked)
FEATURE [Part::Feature] Cut045013
  Placement = pos=(0,0,0) rot=(0,0,-1;1.74533rad)
  shape: bbox 20 x 10 x 20 mm, 7 faces (baked)
FEATURE [Part::Feature] Cut045014
  Placement = pos=(0,0,0) rot=(0,0,-1;1.39626rad)
  shape: bbox 22.21 x 9.894 x 20 mm, 7 faces (baked)
FEATURE [Part::Feature] Cut045015
  Placement = pos=(0,0,0) rot=(0,0,-1;1.0472rad)
  shape: bbox 21.75 x 12.86 x 20 mm, 7 faces (baked)
FEATURE [Part::Feature] Cut045016
  Placement = pos=(0,0,0) rot=(0,0,-1;0.698132rad)
  shape: bbox 18.66 x 17.32 x 20 mm, 7 faces (baked)
FEATURE [Part::Feature] Cut045017
  Placement = pos=(0,0,0) rot=(0,0,-1;0.349066rad)
  shape: bbox 13.32 x 19.7 x 20 mm, 7 faces (baked)
FEATURE [Part::MultiFuse] Fusion095
  Shapes = -> [Cut045001,Cut045008,Cut045010,Cut045009,Cut045005,Cut045003,Cut045006,Cut045002,Cut045004,Cut045007,Cut045016,Cut045017,Cut045011,Cut045012,Cut045013,Cut045014,Cut045015,Cut045]
FEATURE [Part::Cut] Cut045018
  Base = -> Cut044
  Placement = pos=(72,-7,15) rot=(0,1,0;1.5708rad)
  Tool = -> Fusion095
FEATURE [Part::Cut] Cut045019  label="Wheel with Spokes AB"
  Base = -> Cut009
  Tool = -> Cut045018
FEATURE [Part::Box] Box028  label="Cube027"
  AttacherType = Attacher::AttachEngine3D
  Height = 5
  Length = 2
  Placement = pos=(37.5,-9,-2) rot=(0,0,1;0rad)
  Width = 12
FEATURE [Part::Box] Box029  label="Cube028"
  AttacherType = Attacher::AttachEngine3D
  Height = 50
  Length = 47
  Placement = pos=(-9,-8,0) rot=(0,0,1;0rad)
  Width = 12
FEATURE [Part::Box] Box030  label="Cube029"
  AttacherType = Attacher::AttachEngine3D
  Height = 55
  Length = 53
  Placement = pos=(-12,-8,-2.5) rot=(0,0,1;0rad)
  Width = 11
FEATURE [Part::Cylinder] Cylinder064  label="Cylinder160"
  Angle = 360
  AttacherType = Attacher::AttachEngine3D
  Height = 50
  Radius = 7
FEATURE [Part::Cut] Cut045020
  Base = -> Box030
  Tool = -> Box029
FEATURE [Part::Box] Box031  label="Cube030"
  AttacherType = Attacher::AttachEngine3D
  Height = 55
  Length = 53
  Placement = pos=(-12,3,-2.5) rot=(0,0,1;0rad)
  Width = 7
FEATURE [Part::Fuse] Fusion096
  Base = -> Cut045020
  Tool = -> Box031
FEATURE [Part::Box] Box032  label="Battery Base"
  AttacherType = Attacher::AttachEngine3D
  Height = 50
  Length = 56
  Placement = pos=(-14,3,-1) rot=(0,0,1;0rad)
  Width = 7
FEATURE [Part::Box] Box033  label="Cube031"
  AttacherType = Attacher::AttachEngine3D
  Height = 30
  Length = 10
  Placement = pos=(-14,-25,9) rot=(0,0,1;0rad)
  Width = 10
FEATURE [Part::Cylinder] Cylinder065  label="Cylinder161"
  Angle = 360
  AttacherType = Attacher::AttachEngine3D
  Height = 43.5
  Placement = pos=(4,0,2) rot=(0,0,1;0rad)
  Radius = 4.8
FEATURE [Part::Cylinder] Cylinder066  label="Cylinder162"
  Angle = 360
  AttacherType = Attacher::AttachEngine3D
  Height = 1.6
  Placement = pos=(4,0,44) rot=(0,0,1;0rad)
  Radius = 1.65
FEATURE [Part::Fuse] Fusion097
  Base = -> Cylinder065
  Tool = -> Cylinder066
FEATURE [Part::Cylinder] Cylinder067  label="Cylinder163"
  Angle = 360
  AttacherType = Attacher::AttachEngine3D
  Height = 43.5
  Placement = pos=(14,0,2) rot=(0,0,1;0rad)
  Radius = 4.8
FEATURE [Part::Cylinder] Cylinder068  label="Cylinder164"
  Angle = 360
  AttacherType = Attacher::AttachEngine3D
  Height = 1.6
  Placement = pos=(14,0,44) rot=(0,0,1;0rad)
  Radius = 1.65
FEATURE [Part::Fuse] Fusion098
  Base = -> Cylinder067
  Tool = -> Cylinder068
FEATURE [Part::Cylinder] Cylinder069  label="Cylinder165"
  Angle = 360
  AttacherType = Attacher::AttachEngine3D
  Height = 43.5
  Placement = pos=(24,0,2) rot=(0,0,1;0rad)
  Radius = 4.8
FEATURE [Part::Cylinder] Cylinder070  label="Cylinder166"
  Angle = 360
  AttacherType = Attacher::AttachEngine3D
  Height = 1.6
  Placement = pos=(24,0,44) rot=(0,0,1;0rad)
  Radius = 1.65
FEATURE [Part::Fuse] Fusion099
  Base = -> Cylinder069
  Tool = -> Cylinder070
FEATURE [Part::Cylinder] Cylinder071  label="Cylinder167"
  Angle = 360
  AttacherType = Attacher::AttachEngine3D
  Height = 43.5
  Placement = pos=(34,0,2) rot=(0,0,1;0rad)
  Radius = 4.8
FEATURE [Part::Cylinder] Cylinder072  label="Cylinder168"
  Angle = 360
  AttacherType = Attacher::AttachEngine3D
  Height = 1.6
  Placement = pos=(34,0,44) rot=(0,0,1;0rad)
  Radius = 1.65
FEATURE [Part::Fuse] Fusion100
  Base = -> Cylinder071
  Tool = -> Cylinder072
FEATURE [Part::Cylinder] Cylinder073  label="Cylinder169"
  Angle = 360
  AttacherType = Attacher::AttachEngine3D
  Height = 43.5
  Placement = pos=(-6,0,2) rot=(0,0,1;0rad)
  Radius = 4.8
FEATURE [Part::Cylinder] Cylinder074  label="Cylinder170"
  Angle = 360
  AttacherType = Attacher::AttachEngine3D
  Height = 1.6
  Placement = pos=(-6,0,44) rot=(0,0,1;0rad)
  Radius = 1.65
FEATURE [Part::Fuse] Fusion101
  Base = -> Cylinder073
  Tool = -> Cylinder074
FEATURE [Part::MultiFuse] Fusion102  label="AAA Batts001"
  Shapes = -> [Fusion101,Fusion097,Fusion098,Fusion099,Fusion100]
FEATURE [Part::Cylinder] Cylinder075  label="Cylinder171"
  Angle = 360
  AttacherType = Attacher::AttachEngine3D
  Height = 10
  Placement = pos=(-9,-20,4) rot=(0,0,1;0rad)
  Radius = 2.75
FEATURE [Part::Cylinder] Cylinder076  label="Cylinder172"
  Angle = 360
  AttacherType = Attacher::AttachEngine3D
  Height = 27
  Placement = pos=(-9,-20,14) rot=(0,0,1;0rad)
  Radius = 2.5
FEATURE [Part::Fuse] Fusion103  label="phototransistor hole"
  Base = -> Cylinder075
  Tool = -> Cylinder076
FEATURE [Part::Cut] Cut045021  label="Phototransistor holder"
  Base = -> Box033
  Tool = -> Fusion103
FEATURE [Part::Fuse] Fusion104  label="Switch Mount with phototransistor hole"
  Base = -> Cut043
  Tool = -> Cut045021
FEATURE [Part::Cut] Cut045022
  Base = -> Box032
  Tool = -> Fusion102
FEATURE [Part::Box] Box034  label="Cube032"
  AttacherType = Attacher::AttachEngine3D
  Height = 2.5
  Length = 55
  Placement = pos=(-13,-9,-1) rot=(0,0,1;0rad)
  Width = 12
FEATURE [Part::Box] Box035  label="Cube033"
  AttacherType = Attacher::AttachEngine3D
  Height = 2.5
  Length = 55
  Placement = pos=(-13,-9,46.5) rot=(0,0,1;0rad)
  Width = 12
FEATURE [Part::Box] Box036  label="Cube034"
  AttacherType = Attacher::AttachEngine3D
  Height = 50
  Length = 2
  Placement = pos=(-14,-9,-1) rot=(0,0,1;0rad)
  Width = 12
FEATURE [Part::Box] Box037  label="Cube035"
  AttacherType = Attacher::AttachEngine3D
  Height = 50
  Length = 2
  Placement = pos=(40,-9,-1) rot=(0,0,1;0rad)
  Width = 12
FEATURE [Part::MultiFuse] Fusion105
  Shapes = -> [Box034,Box036,Box037,Box035]
FEATURE [Part::Box] Box038  label="Cube036"
  AttacherType = Attacher::AttachEngine3D
  Height = 5
  Length = 2
  Placement = pos=(-10.5,-9,46) rot=(0,0,1;0rad)
  Width = 12
FEATURE [Part::Box] Box039  label="Cube037"
  AttacherType = Attacher::AttachEngine3D
  Height = 5
  Length = 2
  Placement = pos=(-10.5,-9,-2) rot=(0,0,1;0rad)
  Width = 12
FEATURE [Part::MultiFuse] Fusion106
  Shapes = -> [Box039,Box038,Box028,Box007]
FEATURE [Part::MultiFuse] Fusion107
  Shapes = -> [Box003,Box004,Box005,Box008]
FEATURE [Part::Cut] Cut045023
  Base = -> Fusion105
  Tool = -> Fusion106
FEATURE [Part::Cut] Cut045024
  Base = -> Cut045023
  Tool = -> Fusion107
FEATURE [Part::Box] Box040  label="Cube038"
  AttacherType = Attacher::AttachEngine3D
  Height = 1.6
  Length = 30
  Placement = pos=(-56,-15.5,-6) rot=(0,0,1;0rad)
  Width = 15
FEATURE [Part::Box] Box041  label="Cube039"
  AttacherType = Attacher::AttachEngine3D
  Height = 10
  Length = 14
  Placement = pos=(-56,-10.5,-4.5) rot=(0,0,1;0rad)
  Width = 6
FEATURE [Part::Box] Box042  label="Cube040"
  AttacherType = Attacher::AttachEngine3D
  Height = 10
  Length = 5.3
  Placement = pos=(-51.7,-11.5,-4.5) rot=(0,0,1;0rad)
  Width = 8
FEATURE [Part::Cut] Cut045025
  Base = -> Box041
  Tool = -> Box042
FEATURE [Part::Fuse] Fusion108  label="Spoke Sensor PCB"
  Base = -> Box040
  Tool = -> Cut045025
FEATURE [Part::Cylinder] Cylinder077  label="Cylinder173"
  Angle = 360
  AttacherType = Attacher::AttachEngine3D
  Height = 14.5
  Placement = pos=(-43.6,-2.4,-9) rot=(0,0,1;0rad)
  Radius = 0.8
FEATURE [Part::Cylinder] Cylinder078  label="Cylinder174"
  Angle = 360
  AttacherType = Attacher::AttachEngine3D
  Height = 14.5
  Placement = pos=(-43.6,-13.8,-9) rot=(0,0,1;0rad)
  Radius = 0.8
FEATURE [Part::Fuse] Fusion109
  Base = -> Cylinder077
  Tool = -> Cylinder078
FEATURE [Part::Cut] Cut045026  label="Spoke Sensor PCB001"
  Base = -> Fusion108
  Tool = -> Fusion109
FEATURE [Part::Cylinder] Cylinder079  label="Cylinder175"
  Angle = 360
  AttacherType = Attacher::AttachEngine3D
  Height = 14.5
  Placement = pos=(-43.6,-2.4,-18) rot=(0,0,1;0rad)
  Radius = 0.8
FEATURE [Part::Cylinder] Cylinder080  label="Cylinder176"
  Angle = 360
  AttacherType = Attacher::AttachEngine3D
  Height = 14.5
  Placement = pos=(-43.6,-13.8,-18) rot=(0,0,1;0rad)
  Radius = 0.8
FEATURE [Part::Fuse] Fusion110  label="Batt Holder"
  Base = -> Cut045022
  Tool = -> Cut045024
FEATURE [Part::Box] Box043  label="Cube041"
  AttacherType = Attacher::AttachEngine3D
  Height = 4
  Length = 12
  Placement = pos=(-50,-16.75,-17) rot=(0,0,1;0rad)
  Width = 23.75
FEATURE [Part::Cone] Cone
  Angle = 360
  AttacherType = Attacher::AttachEngine3D
  Height = 1.5
  Placement = pos=(-43.6,-2.4,-13) rot=(0,0,1;0rad)
  Radius1 = 2.75
  Radius2 = 1.25
FEATURE [Part::Cone] Cone001
  Angle = 360
  AttacherType = Attacher::AttachEngine3D
  Height = 1.5
  Placement = pos=(-43.6,-13.8,-13) rot=(0,0,1;0rad)
  Radius1 = 2.75
  Radius2 = 1.25
FEATURE [Part::Fuse] Fusion111
  Base = -> Cone
  Tool = -> Cone001
FEATURE [Part::Fuse] Fusion113
  Base = -> Cylinder079
  Tool = -> Cylinder080
FEATURE [Part::Cylinder] Cylinder081  label="Cylinder177"
  Angle = 360
  AttacherType = Attacher::AttachEngine3D
  Height = 14.5
  Placement = pos=(-43.6,-2.4,-18) rot=(0,0,1;0rad)
  Radius = 0.8
FEATURE [Part::Cylinder] Cylinder082  label="Cylinder178"
  Angle = 360
  AttacherType = Attacher::AttachEngine3D
  Height = 14.5
  Placement = pos=(-43.6,-13.8,-18) rot=(0,0,1;0rad)
  Radius = 0.8
FEATURE [Part::Box] Box044  label="Cube042"
  AttacherType = Attacher::AttachEngine3D
  Height = 4
  Length = 12
  Placement = pos=(-50,-16.75,-17) rot=(0,0,1;0rad)
  Width = 26.75
FEATURE [Part::Chamfer] Chamfer001
  Base = -> Box044
  Edges = 1 edges r=7: [Edge3]
FEATURE [Part::Cone] Cone002
  Angle = 360
  AttacherType = Attacher::AttachEngine3D
  Height = 1.5
  Placement = pos=(-43.6,-2.4,-13) rot=(0,0,1;0rad)
  Radius1 = 2.75
  Radius2 = 1.25
FEATURE [Part::Cone] Cone003
  Angle = 360
  AttacherType = Attacher::AttachEngine3D
  Height = 1.5
  Placement = pos=(-43.6,-13.8,-13) rot=(0,0,1;0rad)
  Radius1 = 2.75
  Radius2 = 1.25
FEATURE [Part::Fuse] Fusion114
  Base = -> Cone002
  Tool = -> Cone003
FEATURE [Part::Fuse] Fusion115
  Base = -> Chamfer001
  Tool = -> Fusion114
FEATURE [Part::Fuse] Fusion116
  Base = -> Cylinder081
  Tool = -> Cylinder082
FEATURE [Part::Cut] Cut045028
  Base = -> Fusion115
  Tool = -> Fusion116
FEATURE [Part::Mirroring] Part__Mirroring005  label="Cut045028 (Mirror #6)"
  Base = (0,0,0)
  Normal = (1,0,0)
  Placement = pos=(27,0,0) rot=(0,0,1;0rad)
  Source = -> Cut045028
FEATURE [App::DocumentObjectGroup] Group  label="Older version parts"
  Group = -> [Compound,Compound001,Compound002,Cylinder064,Cylinder010,Cylinder011,Fusion096,Part__Mirroring,Fusion054,Part__Mirroring004,Cut014,Cut015,Cut016,Cut017,Box012,Box013,Box010,Part__Mirroring005,Part__Mirroring003]
FEATURE [Part::Box] Box045  label="Cube043"
  AttacherType = Attacher::AttachEngine3D
  Height = 5
  Length = 2
  Placement = pos=(28,-9,-2) rot=(0,0,1;0rad)
  Width = 12
FEATURE [Part::Box] Box046  label="Cube044"
  AttacherType = Attacher::AttachEngine3D
  Height = 5
  Length = 2
  Placement = pos=(18.5,-9,46) rot=(0,0,1;0rad)
  Width = 12
FEATURE [Part::Box] Box047  label="Cube045"
  AttacherType = Attacher::AttachEngine3D
  Height = 5
  Length = 2
  Placement = pos=(-2,-9,46) rot=(0,0,1;0rad)
  Width = 12
FEATURE [Part::Box] Box048  label="Cube046"
  AttacherType = Attacher::AttachEngine3D
  Height = 5
  Length = 2
  Placement = pos=(37.5,-9,46) rot=(0,0,1;0rad)
  Width = 12
FEATURE [Part::Box] Box049  label="Cube047"
  AttacherType = Attacher::AttachEngine3D
  Height = 5
  Length = 2
  Placement = pos=(8,-9,-2) rot=(0,0,1;0rad)
  Width = 12
FEATURE [Part::Box] Box050  label="Motor Mount Left001"
  AttacherType = Attacher::AttachEngine3D
  Height = 16
  Length = 4
  Placement = pos=(69,-13,7) rot=(0,0,1;0rad)
  Width = 20
FEATURE [Part::Box] Box051  label="Motor Mount Right001"
  AttacherType = Attacher::AttachEngine3D
  Height = 16
  Length = 4
  Placement = pos=(-46,-13,7) rot=(0,0,1;0rad)
  Width = 20
FEATURE [Part::Box] Box052  label="Motor Support Right001"
  AttacherType = Attacher::AttachEngine3D
  Height = 16
  Length = 10
  Placement = pos=(-25,-1,7) rot=(0,0,1;0rad)
  Width = 8
FEATURE [Part::Box] Box053  label="Motor Support Left001"
  AttacherType = Attacher::AttachEngine3D
  Height = 16
  Length = 10
  Placement = pos=(43,-1,7) rot=(0,0,1;0rad)
  Width = 8
FEATURE [Part::Box] Box054  label="Cube014 Arduino Support cube001"
  AttacherType = Attacher::AttachEngine3D
  Height = 67
  Length = 55
  Placement = pos=(-13,5,-68) rot=(0,0,1;0rad)
  Width = 5
FEATURE [Part::Box] Box055  label="Cube048"
  AttacherType = Attacher::AttachEngine3D
  Height = 117
  Length = 33
  Placement = pos=(-46,7,-68) rot=(0,0,1;0rad)
  Width = 3
FEATURE [Part::Box] Box056  label="Cube049"
  AttacherType = Attacher::AttachEngine3D
  Height = 117
  Length = 31
  Placement = pos=(42,7,-68) rot=(0,0,1;0rad)
  Width = 3
FEATURE [Part::Cylinder] Cylinder083  label="Cylinder179"
  Angle = 360
  AttacherType = Attacher::AttachEngine3D
  Height = 28
  Placement = pos=(48,20,-10) rot=(1,0,0;1.5708rad)
  Radius = 1.6
FEATURE [Part::Cylinder] Cylinder084  label="Cylinder180"
  Angle = 360
  AttacherType = Attacher::AttachEngine3D
  Height = 28
  Placement = pos=(48,20,-17) rot=(1,0,0;1.5708rad)
  Radius = 1.6
FEATURE [Part::Cylinder] Cylinder085  label="Cylinder181"
  Angle = 360
  AttacherType = Attacher::AttachEngine3D
  Height = 28
  Placement = pos=(55,20,-17) rot=(1,0,0;1.5708rad)
  Radius = 1.6
FEATURE [Part::Cylinder] Cylinder086  label="Cylinder182"
  Angle = 360
  AttacherType = Attacher::AttachEngine3D
  Height = 28
  Placement = pos=(55,20,-10) rot=(1,0,0;1.5708rad)
  Radius = 1.6
FEATURE [Part::MultiFuse] Fusion117  label="Mount holes top left001"
  Placement = pos=(-1,0,46) rot=(0,0,1;0rad)
  Shapes = -> [Cylinder084,Cylinder085,Cylinder086,Cylinder083]
FEATURE [Part::MultiFuse] Fusion118  label="Mount holes top right001"
  Placement = pos=(-71,0,46) rot=(0,0,1;0rad)
  Shapes = -> [Cylinder084,Cylinder085,Cylinder086,Cylinder083]
FEATURE [Part::Cylinder] Cylinder087  label="Cylinder183"
  Angle = 360
  AttacherType = Attacher::AttachEngine3D
  Height = 10
  Placement = pos=(0,18,29) rot=(0,0,1;0rad)
  Radius = 2.25
FEATURE [Part::Cylinder] Cylinder088  label="Cylinder184"
  Angle = 360
  AttacherType = Attacher::AttachEngine3D
  Height = 10
  Placement = pos=(4.5,18,32) rot=(0,0,1;0rad)
  Radius = 1
FEATURE [Part::Cylinder] Cylinder089  label="Cylinder185"
  Angle = 360
  AttacherType = Attacher::AttachEngine3D
  Height = 10
  Placement = pos=(-4.5,18,32) rot=(0,0,1;0rad)
  Radius = 1
FEATURE [Part::Fuse] Fusion119  label="Mounting Screw Holes002"
  Base = -> Cylinder088
  Tool = -> Cylinder089
FEATURE [Part::Fuse] Fusion120  label="Motor Holes Left001"
  Base = -> Cylinder087
  Placement = pos=(37,-7,-3) rot=(0.57735,0.57735,0.57735;2.0944rad)
  Tool = -> Fusion119
FEATURE [Part::Cylinder] Cylinder090  label="Cylinder186"
  Angle = 360
  AttacherType = Attacher::AttachEngine3D
  Height = 10
  Placement = pos=(0,18,29) rot=(0,0,1;0rad)
  Radius = 2.25
FEATURE [Part::Cylinder] Cylinder091  label="Cylinder187"
  Angle = 360
  AttacherType = Attacher::AttachEngine3D
  Height = 10
  Placement = pos=(4.5,18,32) rot=(0,0,1;0rad)
  Radius = 1
FEATURE [Part::Cylinder] Cylinder092  label="Cylinder188"
  Angle = 360
  AttacherType = Attacher::AttachEngine3D
  Height = 10
  Placement = pos=(-4.5,18,32) rot=(0,0,1;0rad)
  Radius = 1
FEATURE [Part::Fuse] Fusion121  label="Mounting Screw Holes003"
  Base = -> Cylinder091
  Tool = -> Cylinder092
FEATURE [Part::Fuse] Fusion122  label="Motor Holes Right001"
  Base = -> Cylinder090
  Placement = pos=(-79,-7,-3) rot=(0.57735,0.57735,0.57735;2.0944rad)
  Tool = -> Fusion121
FEATURE [Part::Cylinder] Cylinder093  label="Cylinder189"
  Angle = 360
  AttacherType = Attacher::AttachEngine3D
  Height = 28
  Placement = pos=(40.7,0,-10.3) rot=(1,0,0;1.5708rad)
  Radius = 1.6
FEATURE [Part::Cylinder] Cylinder094  label="Cylinder190"
  Angle = 360
  AttacherType = Attacher::AttachEngine3D
  Height = 28
  Placement = pos=(-2.4,0,-59.8) rot=(1,0,0;1.5708rad)
  Radius = 1.6
FEATURE [Part::Cylinder] Cylinder095  label="Cylinder191"
  Angle = 360
  AttacherType = Attacher::AttachEngine3D
  Height = 28
  Placement = pos=(-5,0,-9) rot=(1,0,0;1.5708rad)
  Radius = 1.6
FEATURE [Part::Cylinder] Cylinder096  label="Cylinder192"
  Angle = 360
  AttacherType = Attacher::AttachEngine3D
  Height = 28
  Placement = pos=(25.5,0,-59.8) rot=(1,0,0;1.5708rad)
  Radius = 1.6
FEATURE [Part::Fuse] Fusion123
  Base = -> Cylinder094
  Tool = -> Cylinder095
FEATURE [Part::Fuse] Fusion124
  Base = -> Cylinder093
  Tool = -> Cylinder096
FEATURE [Part::Fuse] Fusion125  label="Screw holes on Arduino Duo002"
  Base = -> Fusion123
  Tool = -> Fusion124
FEATURE [Part::Mirroring] Part__Mirroring006  label="Screw holes on Arduino Duo (Mirror #1)002"
  Base = (0,0,0)
  Normal = (0,0,1)
  Placement = pos=(-4,10,-67) rot=(0,0,1;0rad)
  Source = -> Fusion125
FEATURE [Part::Mirroring] Part__Mirroring007  label="Screw holes on Arduino Duo (Mirror #1)001 (Mirror #4)001"
  Base = (0,0,0)
  Normal = (1,0,0)
  Placement = pos=(27,0,-6) rot=(0,0,1;0rad)
  Source = -> Part__Mirroring006
FEATURE [Part::Box] Box057  label="Cube050"
  AttacherType = Attacher::AttachEngine3D
  Height = 50
  Length = 47
  Placement = pos=(-9,-8,0) rot=(0,0,1;0rad)
  Width = 12
FEATURE [Part::Box] Box058  label="Cube051"
  AttacherType = Attacher::AttachEngine3D
  Height = 55
  Length = 53
  Placement = pos=(-12,-8,-2.5) rot=(0,0,1;0rad)
  Width = 11
FEATURE [Part::Cut] Cut045029
  Base = -> Box058
  Tool = -> Box057
FEATURE [Part::Box] Box059  label="Cube052"
  AttacherType = Attacher::AttachEngine3D
  Height = 5
  Length = 3
  Placement = pos=(35,-9,-4) rot=(0,0,1;0rad)
  Width = 12
FEATURE [Part::Cut] Cut045030
  Base = -> Cut045029
  Placement = pos=(-9,10,-58) rot=(1,0,0;1.5708rad)
  Tool = -> Box059
FEATURE [Part::Cut] Cut045031
  Base = -> Cut045029
  Placement = pos=(36.7,10,-56.7) rot=(1,0,0;1.5708rad)
  Tool = -> Box059
FEATURE [Part::Cut] Cut045032
  Base = -> Cut045029
  Placement = pos=(-6.4,10,-7.2) rot=(1,0,0;1.5708rad)
  Tool = -> Box059
FEATURE [Part::Cut] Cut045033
  Base = -> Cut045029
  Placement = pos=(21.5,10,-7.2) rot=(1,0,0;1.5708rad)
  Tool = -> Box059
FEATURE [Part::MultiFuse] Fusion126
  Shapes = -> [Cut045030,Cut045033,Cut045031,Cut045032]
FEATURE [Part::Mirroring] Part__Mirroring008  label="Hex Holes001"
  Base = (0,0,0)
  Normal = (1,0,0)
  Placement = pos=(27,0,-6) rot=(0,0,1;0rad)
  Source = -> Fusion126
FEATURE [Part::Box] Box060  label="Cube053"
  AttacherType = Attacher::AttachEngine3D
  Height = 5
  Length = 2
  Placement = pos=(37.5,-9,-2) rot=(0,0,1;0rad)
  Width = 12
FEATURE [Part::Box] Box061  label="Battery Base001"
  AttacherType = Attacher::AttachEngine3D
  Height = 50
  Length = 55
  Placement = pos=(-13,3,-1) rot=(0,0,1;0rad)
  Width = 7
FEATURE [Part::Cylinder] Cylinder097  label="Cylinder193"
  Angle = 360
  AttacherType = Attacher::AttachEngine3D
  Height = 42
  Radius = 4.8
FEATURE [Part::Cylinder] Cylinder098  label="Cylinder194"
  Angle = 360
  AttacherType = Attacher::AttachEngine3D
  Height = 1.6
  Placement = pos=(0,0,42) rot=(0,0,1;0rad)
  Radius = 1.65
FEATURE [Part::Fuse] Fusion127
  Base = -> Cylinder097
  Placement = pos=(2,0,0) rot=(0,0,1;0rad)
  Tool = -> Cylinder098
FEATURE [Part::Cylinder] Cylinder099  label="Cylinder195"
  Angle = 360
  AttacherType = Attacher::AttachEngine3D
  Height = 42
  Radius = 4.8
FEATURE [Part::Cylinder] Cylinder100  label="Cylinder196"
  Angle = 360
  AttacherType = Attacher::AttachEngine3D
  Height = 1.6
  Placement = pos=(0,0,42) rot=(0,0,1;0rad)
  Radius = 1.65
FEATURE [Part::Fuse] Fusion128
  Base = -> Cylinder099
  Placement = pos=(12,0,0) rot=(0,0,1;0rad)
  Tool = -> Cylinder100
FEATURE [Part::Cylinder] Cylinder101  label="Cylinder197"
  Angle = 360
  AttacherType = Attacher::AttachEngine3D
  Height = 42
  Radius = 4.8
FEATURE [Part::Cylinder] Cylinder102  label="Cylinder198"
  Angle = 360
  AttacherType = Attacher::AttachEngine3D
  Height = 1.6
  Placement = pos=(0,0,42) rot=(0,0,1;0rad)
  Radius = 1.65
FEATURE [Part::Fuse] Fusion129
  Base = -> Cylinder101
  Placement = pos=(22,0,0) rot=(0,0,1;0rad)
  Tool = -> Cylinder102
FEATURE [Part::Cylinder] Cylinder103  label="Cylinder199"
  Angle = 360
  AttacherType = Attacher::AttachEngine3D
  Height = 42
  Radius = 4.8
FEATURE [Part::Cylinder] Cylinder104  label="Cylinder200"
  Angle = 360
  AttacherType = Attacher::AttachEngine3D
  Height = 1.6
  Placement = pos=(0,0,42) rot=(0,0,1;0rad)
  Radius = 1.65
FEATURE [Part::Fuse] Fusion130
  Base = -> Cylinder103
  Placement = pos=(32,0,0) rot=(0,0,1;0rad)
  Tool = -> Cylinder104
FEATURE [Part::Cylinder] Cylinder105  label="Cylinder201"
  Angle = 360
  AttacherType = Attacher::AttachEngine3D
  Height = 42
  Radius = 4.8
FEATURE [Part::Cylinder] Cylinder106  label="Cylinder202"
  Angle = 360
  AttacherType = Attacher::AttachEngine3D
  Height = 1.6
  Placement = pos=(0,0,42) rot=(0,0,1;0rad)
  Radius = 1.65
FEATURE [Part::Fuse] Fusion131
  Base = -> Cylinder105
  Placement = pos=(-8,0,0) rot=(0,0,1;0rad)
  Tool = -> Cylinder106
FEATURE [Part::MultiFuse] Fusion132  label="AAA Batts002"
  Placement = pos=(2,0,2) rot=(0,0,1;0rad)
  Shapes = -> [Fusion131,Fusion127,Fusion128,Fusion129,Fusion130]
FEATURE [Part::Cut] Cut045034
  Base = -> Box061
  Tool = -> Fusion132
FEATURE [Part::Box] Box062  label="Cube054"
  AttacherType = Attacher::AttachEngine3D
  Height = 2.5
  Length = 55
  Placement = pos=(-13,-9,-1) rot=(0,0,1;0rad)
  Width = 12
FEATURE [Part::Box] Box063  label="Cube055"
  AttacherType = Attacher::AttachEngine3D
  Height = 2.5
  Length = 55
  Placement = pos=(-13,-9,46.5) rot=(0,0,1;0rad)
  Width = 12
FEATURE [Part::Box] Box064  label="Cube056"
  AttacherType = Attacher::AttachEngine3D
  Height = 50
  Length = 2.5
  Placement = pos=(-13,-9,-1) rot=(0,0,1;0rad)
  Width = 12
FEATURE [Part::Box] Box065  label="Cube057"
  AttacherType = Attacher::AttachEngine3D
  Height = 50
  Length = 2.5
  Placement = pos=(39.5,-9,-1) rot=(0,0,1;0rad)
  Width = 12
FEATURE [Part::MultiFuse] Fusion133
  Shapes = -> [Box062,Box064,Box065,Box063]
FEATURE [Part::Box] Box066  label="Cube058"
  AttacherType = Attacher::AttachEngine3D
  Height = 5
  Length = 2
  Placement = pos=(-10.5,-9,46) rot=(0,0,1;0rad)
  Width = 12
FEATURE [Part::Box] Box067  label="Cube059"
  AttacherType = Attacher::AttachEngine3D
  Height = 5
  Length = 2
  Placement = pos=(-10.5,-9,-2) rot=(0,0,1;0rad)
  Width = 12
FEATURE [Part::MultiFuse] Fusion134
  Shapes = -> [Box067,Box066,Box060,Box048]
FEATURE [Part::MultiFuse] Fusion135
  Shapes = -> [Box045,Box046,Box047,Box049]
FEATURE [Part::Cut] Cut045035
  Base = -> Fusion133
  Tool = -> Fusion134
FEATURE [Part::Cut] Cut045036
  Base = -> Cut045035
  Tool = -> Fusion135
FEATURE [Part::Cylinder] Cylinder107  label="Cylinder203"
  Angle = 360
  AttacherType = Attacher::AttachEngine3D
  Height = 14.5
  Placement = pos=(-43.6,-2.4,-15) rot=(0,0,1;0rad)
  Radius = 0.8
FEATURE [Part::Cylinder] Cylinder108  label="Cylinder204"
  Angle = 360
  AttacherType = Attacher::AttachEngine3D
  Height = 14.5
  Placement = pos=(-43.6,-13.8,-15) rot=(0,0,1;0rad)
  Radius = 0.8
FEATURE [Part::Fuse] Fusion136
  Base = -> Cut045034
  Tool = -> Cut045036
FEATURE [Part::Box] Box068  label="Cube060"
  AttacherType = Attacher::AttachEngine3D
  Height = 4
  Length = 12
  Placement = pos=(-50,-16.75,-14) rot=(0,0,1;0rad)
  Width = 26.75
FEATURE [Part::Chamfer] Chamfer002
  Base = -> Box068
  Edges = 1 edges r=7: [Edge3]
FEATURE [Part::Cone] Cone004
  Angle = 360
  AttacherType = Attacher::AttachEngine3D
  Height = 1.5
  Placement = pos=(-43.6,-2.4,-10) rot=(0,0,1;0rad)
  Radius1 = 2.75
  Radius2 = 1.25
FEATURE [Part::Cone] Cone005
  Angle = 360
  AttacherType = Attacher::AttachEngine3D
  Height = 1.5
  Placement = pos=(-43.6,-13.8,-10) rot=(0,0,1;0rad)
  Radius1 = 2.75
  Radius2 = 1.25
FEATURE [Part::Fuse] Fusion137
  Base = -> Cone004
  Tool = -> Cone005
FEATURE [Part::Fuse] Fusion138
  Base = -> Chamfer002
  Tool = -> Fusion137
FEATURE [Part::Fuse] Fusion139
  Base = -> Cylinder107
  Tool = -> Cylinder108
FEATURE [Part::Cut] Cut045037
  Base = -> Fusion138
  Tool = -> Fusion139
FEATURE [Part::Cylinder] Cylinder109  label="Cylinder205"
  Angle = 360
  AttacherType = Attacher::AttachEngine3D
  Height = 14.5
  Placement = pos=(-43.6,-2.4,-15) rot=(0,0,1;0rad)
  Radius = 0.8
FEATURE [Part::Cylinder] Cylinder110  label="Cylinder206"
  Angle = 360
  AttacherType = Attacher::AttachEngine3D
  Height = 14.5
  Placement = pos=(-43.6,-13.8,-15) rot=(0,0,1;0rad)
  Radius = 0.8
FEATURE [Part::Box] Box069  label="Cube061"
  AttacherType = Attacher::AttachEngine3D
  Height = 4
  Length = 12
  Placement = pos=(-50,-16.75,-14) rot=(0,0,1;0rad)
  Width = 26.75
FEATURE [Part::Chamfer] Chamfer003
  Base = -> Box069
  Edges = 1 edges r=7: [Edge3]
FEATURE [Part::Cone] Cone006
  Angle = 360
  AttacherType = Attacher::AttachEngine3D
  Height = 1.5
  Placement = pos=(-43.6,-2.4,-10) rot=(0,0,1;0rad)
  Radius1 = 2.75
  Radius2 = 1.25
FEATURE [Part::Cone] Cone007
  Angle = 360
  AttacherType = Attacher::AttachEngine3D
  Height = 1.5
  Placement = pos=(-43.6,-13.8,-10) rot=(0,0,1;0rad)
  Radius1 = 2.75
  Radius2 = 1.25
FEATURE [Part::Fuse] Fusion140
  Base = -> Cone006
  Tool = -> Cone007
FEATURE [Part::Fuse] Fusion141
  Base = -> Chamfer003
  Tool = -> Fusion140
FEATURE [Part::Fuse] Fusion142
  Base = -> Cylinder109
  Tool = -> Cylinder110
FEATURE [Part::Cut] Cut045038
  Base = -> Fusion141
  Tool = -> Fusion142
FEATURE [Part::Mirroring] Part__Mirroring009  label="Cut045028 (Mirror #6)001"
  Base = (0,0,0)
  Normal = (1,0,0)
  Placement = pos=(27,0,0) rot=(0,0,1;0rad)
  Source = -> Cut045038
FEATURE [Part::Cut] Cut045039
  Base = -> Box050
  Tool = -> Fusion120
FEATURE [Part::Cut] Cut045040
  Base = -> Box051
  Tool = -> Fusion122
FEATURE [Part::MultiFuse] Fusion143
  Shapes = -> [Box054,Box055,Box056]
FEATURE [Part::Fuse] Fusion144
  Base = -> Fusion136
  Tool = -> Fusion143
FEATURE [Part::MultiFuse] Fusion145
  Shapes = -> [Fusion144,Cut045040,Cut045039]
FEATURE [Part::MultiFuse] Fusion146
  Shapes = -> [Fusion145,Part__Mirroring009,Cut045037]
FEATURE [Part::Cut] Cut045041
  Base = -> Fusion146
  Tool = -> Fusion117
FEATURE [Part::Cut] Cut045042
  Base = -> Cut045041
  Tool = -> Fusion118
FEATURE [Part::Cut] Cut045043
  Base = -> Cut045042
  Tool = -> Part__Mirroring007
FEATURE [Part::Cut] Cut045044
  Base = -> Cut045043
  Tool = -> Part__Mirroring008
FEATURE [Part::MultiFuse] Fusion147
  Shapes = -> [Cut045044,Box053,Box052]
FEATURE [Part::Chamfer] Chamfer004
  Base = -> Fusion147
  Edges = 1 edges r=25: [Edge43]
FEATURE [Part::Chamfer] Chamfer005
  Base = -> Chamfer004
  Edges = 1 edges r=25: [Edge225]
FEATURE [Part::Chamfer] Chamfer006
  Base = -> Chamfer005
  Edges = 1 edges r=30: [Edge58]
FEATURE [Part::Chamfer] Chamfer007
  Base = -> Chamfer006
  Edges = 1 edges r=30: [Edge148]
FEATURE [Part::Fillet] Fillet
  Base = -> Chamfer007
  Edges = 1 edges r=2: [Edge233]
FEATURE [Part::Fillet] Fillet001
  Base = -> Fillet
  Edges = 1 edges r=2: [Edge6]
FEATURE [Part::Fillet] Fillet002
  Base = -> Fillet001
  Edges = 1 edges r=2: [Edge2]
FEATURE [Part::Fillet] Fillet003
  Base = -> Fillet002
  Edges = 1 edges r=2: [Edge357]
FEATURE [Part::Fillet] Fillet004
  Base = -> Fillet003
  Edges = 1 edges r=2: [Edge6]
FEATURE [Part::Fillet] Fillet005
  Base = -> Fillet004
  Edges = 1 edges r=2: [Edge2]
FEATURE [Part::Fillet] Fillet006
  Base = -> Fillet005
  Edges = 1 edges r=2: [Edge407]
FEATURE [Part::Fillet] Fillet007
  Base = -> Fillet006
  Edges = 1 edges r=2: [Edge2]
FEATURE [Part::Fillet] Fillet008
  Base = -> Fillet007
  Edges = 1 edges r=2: [Edge369]
FEATURE [Part::Fillet] Fillet009
  Base = -> Fillet008
  Edges = 1 edges r=2: [Edge2]
FEATURE [Part::Cylinder] Cylinder111  label="Cylinder207"
  Angle = 360
  AttacherType = Attacher::AttachEngine3D
  Height = 28
  Placement = pos=(45,6,47) rot=(0.707107,0,0.707107;4.01426rad)
  Radius = 0.5
FEATURE [Part::Cylinder] Cylinder112  label="Cylinder208"
  Angle = 360
  AttacherType = Attacher::AttachEngine3D
  Height = 28
  Placement = pos=(66,6,26) rot=(0.707107,0,0.707107;4.01426rad)
  Radius = 0.5
FEATURE [Part::Cut] Cut045045
  Base = -> Fillet009
  Tool = -> Cylinder111
FEATURE [Part::Cut] Cut045046
  Base = -> Cut045045
  Tool = -> Cylinder112
FEATURE [Part::Cylinder] Cylinder113  label="Cylinder209"
  Angle = 360
  AttacherType = Attacher::AttachEngine3D
  Height = 28
  Placement = pos=(66,6,26) rot=(0.707107,0,0.707107;4.01426rad)
  Radius = 0.5
FEATURE [Part::Mirroring] Part__Mirroring010  label="Cylinder137 (Mirror #7)"
  Base = (0,0,0)
  Normal = (1,0,0)
  Placement = pos=(27,0,0) rot=(0,0,1;0rad)
  Source = -> Cylinder113
FEATURE [Part::Cylinder] Cylinder114  label="Cylinder210"
  Angle = 360
  AttacherType = Attacher::AttachEngine3D
  Height = 28
  Placement = pos=(45,6,47) rot=(0.707107,0,0.707107;4.01426rad)
  Radius = 0.5
FEATURE [Part::Mirroring] Part__Mirroring011  label="Cylinder138 (Mirror #8)"
  Base = (0,0,0)
  Normal = (1,0,0)
  Placement = pos=(27,0,0) rot=(0,0,1;0rad)
  Source = -> Cylinder114
FEATURE [Part::Cut] Cut045047
  Base = -> Cut045046
  Tool = -> Part__Mirroring010
FEATURE [Part::Cut] Cut045048  label="Old Layout"
  Base = -> Cut045047
  Tool = -> Part__Mirroring011
FEATURE [Part::Cylinder] Cylinder115  label="Arduino Cylinder191"
  Angle = 360
  AttacherType = Attacher::AttachEngine3D
  Height = 28
  Placement = pos=(4,11,-8.6) rot=(1,0,0;1.5708rad)
  Radius = 1.6
FEATURE [Part::Cylinder] Cylinder116  label="Arduino Cylinder192"
  Angle = 360
  AttacherType = Attacher::AttachEngine3D
  Height = 28
  Placement = pos=(31.9,11,-8.6) rot=(1,0,0;1.5708rad)
  Radius = 1.6
FEATURE [Part::Cylinder] Cylinder117  label="Arduino Cylinder193"
  Angle = 360
  AttacherType = Attacher::AttachEngine3D
  Height = 28
  Placement = pos=(-11.2,11,-59.4) rot=(1,0,0;1.5708rad)
  Radius = 1.6
FEATURE [Part::Cylinder] Cylinder118  label="Arduino Cylinder194"
  Angle = 360
  AttacherType = Attacher::AttachEngine3D
  Height = 28
  Placement = pos=(37.2,11,-60.5) rot=(1,0,0;1.5708rad)
  Radius = 1.6
FEATURE [Part::Cylinder] Cylinder119  label="Arduino Cylinder195"
  Angle = 360
  AttacherType = Attacher::AttachEngine3D
  Height = 2.5
  Placement = pos=(4,13,-8.6) rot=(1,0,0;1.5708rad)
  Radius = 4
FEATURE [Part::Feature] Box014001
  Placement = pos=(3.88157,4,-2.89487) rot=(0,1,0;1.0472rad)
  shape: bbox 13.66 x 10 x 13.66 mm, 6 faces (baked)
FEATURE [Part::Feature] Box014002
  Placement = pos=(8.88157,4,-5.64487) rot=(0,1,0;2.0944rad)
  shape: bbox 13.66 x 10 x 13.66 mm, 6 faces (baked)
FEATURE [Part::Feature] Box014003
  Placement = pos=(9,4,-11.35) rot=(0,1,0;3.14159rad)
  shape: bbox 10 x 10 x 10 mm, 6 faces (baked)
FEATURE [Part::Feature] Box014004
  Placement = pos=(4.11843,4,-14.3051) rot=(0,1,0;4.18879rad)
  shape: bbox 13.66 x 10 x 13.66 mm, 6 faces (baked)
FEATURE [Part::Feature] Box014005
  Placement = pos=(-0.88157,4,-11.5551) rot=(0,-1,0;1.0472rad)
  shape: bbox 13.66 x 10 x 13.66 mm, 6 faces (baked)
FEATURE [Part::MultiFuse] Fusion148
  Shapes = -> [Box014001,Box014002,Box014004,Box014003,Box014005,Box014]
FEATURE [Part::Cut] Cut045049  label="M3 Nut004"
  Base = -> Cylinder119
  Placement = pos=(0,-3,0) rot=(0,0,1;0rad)
  Tool = -> Fusion148
FEATURE [Part::Box] Box014006  label="Not used Cube001"
  AttacherType = Attacher::AttachEngine3D
  Height = 10
  Length = 10
  Placement = pos=(-1,4,-5.85) rot=(0,0,1;0rad)
  Width = 10
FEATURE [Part::Cylinder] Cylinder120  label="Arduino Cylinder196"
  Angle = 360
  AttacherType = Attacher::AttachEngine3D
  Height = 2.5
  Placement = pos=(4,13,-8.6) rot=(1,0,0;1.5708rad)
  Radius = 4
FEATURE [Part::Feature] Box014007
  Placement = pos=(3.88157,4,-2.89487) rot=(0,1,0;1.0472rad)
  shape: bbox 13.66 x 10 x 13.66 mm, 6 faces (baked)
FEATURE [Part::Feature] Box014008
  Placement = pos=(8.88157,4,-5.64487) rot=(0,1,0;2.0944rad)
  shape: bbox 13.66 x 10 x 13.66 mm, 6 faces (baked)
FEATURE [Part::Feature] Box014009
  Placement = pos=(9,4,-11.35) rot=(0,1,0;3.14159rad)
  shape: bbox 10 x 10 x 10 mm, 6 faces (baked)
FEATURE [Part::Feature] Box014010
  Placement = pos=(4.11843,4,-14.3051) rot=(0,1,0;4.18879rad)
  shape: bbox 13.66 x 10 x 13.66 mm, 6 faces (baked)
FEATURE [Part::Feature] Box014011
  Placement = pos=(-0.88157,4,-11.5551) rot=(0,-1,0;1.0472rad)
  shape: bbox 13.66 x 10 x 13.66 mm, 6 faces (baked)
FEATURE [Part::MultiFuse] Fusion149
  Shapes = -> [Box014007,Box014008,Box014010,Box014009,Box014011,Box014006]
FEATURE [Part::Cut] Cut045050  label="M3 Nut005"
  Base = -> Cylinder120
  Placement = pos=(27.9,-3,0) rot=(0,0,1;0rad)
  Tool = -> Fusion149
FEATURE [Part::Box] Box014012  label="Not used Cube002"
  AttacherType = Attacher::AttachEngine3D
  Height = 10
  Length = 10
  Placement = pos=(-1,4,-5.85) rot=(0,0,1;0rad)
  Width = 10
FEATURE [Part::Cylinder] Cylinder121  label="Arduino Cylinder197"
  Angle = 360
  AttacherType = Attacher::AttachEngine3D
  Height = 2.5
  Placement = pos=(4,13,-8.6) rot=(1,0,0;1.5708rad)
  Radius = 4
FEATURE [Part::Feature] Box014013
  Placement = pos=(3.88157,4,-2.89487) rot=(0,1,0;1.0472rad)
  shape: bbox 13.66 x 10 x 13.66 mm, 6 faces (baked)
FEATURE [Part::Feature] Box014014
  Placement = pos=(8.88157,4,-5.64487) rot=(0,1,0;2.0944rad)
  shape: bbox 13.66 x 10 x 13.66 mm, 6 faces (baked)
FEATURE [Part::Feature] Box014015
  Placement = pos=(9,4,-11.35) rot=(0,1,0;3.14159rad)
  shape: bbox 10 x 10 x 10 mm, 6 faces (baked)
FEATURE [Part::Feature] Box014016
  Placement = pos=(4.11843,4,-14.3051) rot=(0,1,0;4.18879rad)
  shape: bbox 13.66 x 10 x 13.66 mm, 6 faces (baked)
FEATURE [Part::Feature] Box014017
  Placement = pos=(-0.88157,4,-11.5551) rot=(0,-1,0;1.0472rad)
  shape: bbox 13.66 x 10 x 13.66 mm, 6 faces (baked)
FEATURE [Part::MultiFuse] Fusion150
  Shapes = -> [Box014013,Box014014,Box014016,Box014015,Box014017,Box014012]
FEATURE [Part::Cut] Cut045051  label="M3 Nut006"
  Base = -> Cylinder121
  Placement = pos=(-15.2,-3,-50.8) rot=(0,0,1;0rad)
  Tool = -> Fusion150
FEATURE [Part::Box] Box014018  label="Not used Cube003"
  AttacherType = Attacher::AttachEngine3D
  Height = 10
  Length = 10
  Placement = pos=(-1,4,-5.85) rot=(0,0,1;0rad)
  Width = 10
FEATURE [Part::Cylinder] Cylinder122  label="Arduino Cylinder198"
  Angle = 360
  AttacherType = Attacher::AttachEngine3D
  Height = 2.5
  Placement = pos=(4,13,-8.6) rot=(1,0,0;1.5708rad)
  Radius = 4
FEATURE [Part::Feature] Box014019
  Placement = pos=(3.88157,4,-2.89487) rot=(0,1,0;1.0472rad)
  shape: bbox 13.66 x 10 x 13.66 mm, 6 faces (baked)
FEATURE [Part::Feature] Box014020
  Placement = pos=(8.88157,4,-5.64487) rot=(0,1,0;2.0944rad)
  shape: bbox 13.66 x 10 x 13.66 mm, 6 faces (baked)
FEATURE [Part::Feature] Box014021
  Placement = pos=(9,4,-11.35) rot=(0,1,0;3.14159rad)
  shape: bbox 10 x 10 x 10 mm, 6 faces (baked)
FEATURE [Part::Feature] Box014022
  Placement = pos=(4.11843,4,-14.3051) rot=(0,1,0;4.18879rad)
  shape: bbox 13.66 x 10 x 13.66 mm, 6 faces (baked)
FEATURE [Part::Feature] Box014023
  Placement = pos=(-0.88157,4,-11.5551) rot=(0,-1,0;1.0472rad)
  shape: bbox 13.66 x 10 x 13.66 mm, 6 faces (baked)
FEATURE [Part::MultiFuse] Fusion151
  Shapes = -> [Box014019,Box014020,Box014022,Box014021,Box014023,Box014018]
FEATURE [Part::Cut] Cut045052  label="M3 Nut007"
  Base = -> Cylinder122
  Placement = pos=(33.2,-3,-51.9) rot=(0,0,1;0rad)
  Tool = -> Fusion151
FEATURE [Part::Box] Box014024  label="Cube062"
  AttacherType = Attacher::AttachEngine3D
  Height = 67
  Length = 65
  Placement = pos=(-16,-13,-6) rot=(0,0,1;0rad)
  Width = 8
FEATURE [Part::Cut] Cut045053  label="BAtt Holder"
  Base = -> Fusion110
  Tool = -> Box014024
FEATURE [Part::Cylinder] Cylinder123  label="Cylinder211"
  Angle = 360
  AttacherType = Attacher::AttachEngine3D
  Height = 28
  Placement = pos=(45,6,47) rot=(0.707107,0,0.707107;4.01426rad)
  Radius = 0.5
FEATURE [Part::Cylinder] Cylinder124  label="Cylinder212"
  Angle = 360
  AttacherType = Attacher::AttachEngine3D
  Height = 28
  Placement = pos=(66,6,26) rot=(0.707107,0,0.707107;4.01426rad)
  Radius = 0.5
FEATURE [Part::Cylinder] Cylinder125  label="Cylinder213"
  Angle = 360
  AttacherType = Attacher::AttachEngine3D
  Height = 28
  Placement = pos=(45,6,47) rot=(0.707107,0,0.707107;4.01426rad)
  Radius = 0.5
FEATURE [Part::Cylinder] Cylinder126  label="Cylinder214"
  Angle = 360
  AttacherType = Attacher::AttachEngine3D
  Height = 28
  Placement = pos=(66,6,26) rot=(0.707107,0,0.707107;4.01426rad)
  Radius = 0.5
FEATURE [Part::Mirroring] Part__Mirroring012  label="Cylinder211 (Mirror #13)"
  Base = (0,0,0)
  Normal = (1,0,0)
  Placement = pos=(27,0,0) rot=(0,0,1;0rad)
  Source = -> Cylinder125
FEATURE [Part::Mirroring] Part__Mirroring013  label="Cylinder212 (Mirror #14)"
  Base = (0,0,0)
  Normal = (1,0,0)
  Placement = pos=(27,0,0) rot=(0,0,1;0rad)
  Source = -> Cylinder126
FEATURE [Part::Box] Box014025  label="Cube063"
  AttacherType = Attacher::AttachEngine3D
  Height = 14
  Length = 15
  Placement = pos=(-46,4,-27) rot=(0,0,1;0rad)
  Width = 3
FEATURE [Part::Cylinder] Cylinder127  label="Cylinder215"
  Angle = 360
  AttacherType = Attacher::AttachEngine3D
  Height = 10
  Placement = pos=(-39,9,-22) rot=(1,0,0;1.5708rad)
  Radius = 4
FEATURE [Part::Box] Box014026  label="Cube064"
  AttacherType = Attacher::AttachEngine3D
  Height = 9.5
  Length = 15
  Placement = pos=(-46,0,-27) rot=(0,0,1;0rad)
  Width = 3
FEATURE [Part::Cylinder] Cylinder128  label="Cylinder216"
  Angle = 360
  AttacherType = Attacher::AttachEngine3D
  Height = 14
  Placement = pos=(-39,11,-22) rot=(1,0,0;1.5708rad)
  Radius = 1.5
FEATURE [Part::Cut] Cut045054
  Base = -> Box014025
  Tool = -> Cylinder127
FEATURE [Part::Cylinder] Cylinder129  label="Sensor Mount Hole"
  Angle = 360
  AttacherType = Attacher::AttachEngine3D
  Height = 14
  Placement = pos=(-39,11,-22) rot=(1,0,0;1.5708rad)
  Radius = 1.5
FEATURE [Part::Cut] Cut045055  label="Printed Washer"
  Base = -> Box014026
  Tool = -> Cylinder128
FEATURE [Part::Box] Box014027  label="Cube065"
  AttacherType = Attacher::AttachEngine3D
  Height = 23
  Length = 22
  Placement = pos=(-46,4,0) rot=(0,0,1;0rad)
  Width = 3
FEATURE [Part::Cylinder] Cylinder130  label="Cylinder218"
  Angle = 360
  AttacherType = Attacher::AttachEngine3D
  Height = 14
  Placement = pos=(-38,11,4) rot=(1,0,0;1.5708rad)
  Radius = 1.5
FEATURE [Part::Cylinder] Cylinder131  label="Cylinder219"
  Angle = 360
  AttacherType = Attacher::AttachEngine3D
  Height = 14
  Placement = pos=(-28,11,4) rot=(1,0,0;1.5708rad)
  Radius = 1.5
FEATURE [Part::Cylinder] Cylinder132  label="Cylinder220"
  Angle = 360
  AttacherType = Attacher::AttachEngine3D
  Height = 14.5
  Placement = pos=(-53.76,-13.8,-18) rot=(0,0,1;0rad)
  Radius = 0.8
FEATURE [Part::Box] Box014028  label="Cube066"
  AttacherType = Attacher::AttachEngine3D
  Height = 4
  Length = 19
  Placement = pos=(-57,-16.75,-17) rot=(0,0,1;0rad)
  Width = 8.75
FEATURE [Part::Cone] Cone008
  Angle = 360
  AttacherType = Attacher::AttachEngine3D
  Height = 1.5
  Placement = pos=(-53.76,-13.8,-13) rot=(0,0,1;0rad)
  Radius1 = 2.75
  Radius2 = 1.25
FEATURE [Part::Fuse] Fusion152
  Base = -> Fusion111
  Tool = -> Cone008
FEATURE [Part::Fuse] Fusion153
  Base = -> Fusion113
  Tool = -> Cylinder132
FEATURE [Part::Fuse] Fusion154
  Base = -> Box043
  Tool = -> Box014028
FEATURE [Part::Fuse] Fusion155
  Base = -> Cut045054
  Tool = -> Fusion154
FEATURE [Part::Fuse] Fusion156
  Base = -> Fusion152
  Tool = -> Fusion155
FEATURE [Part::Cut] Cut045056
  Base = -> Fusion156
  Tool = -> Fusion153
FEATURE [Part::Chamfer] Chamfer
  Base = -> Cut045056
  Edges = 1 edges r=6.99: [Edge15]
FEATURE [Part::Fillet] Fillet010
  Base = -> Chamfer
  Edges = 1 edges r=1: [Edge51]
FEATURE [Part::Fillet] Fillet011
  Base = -> Fillet010
  Edges = 1 edges r=1: [Edge11]
FEATURE [Part::Fillet] Fillet012
  Base = -> Fillet011
  Edges = 1 edges r=1: [Edge37]
FEATURE [Part::Fillet] Fillet013
  Base = -> Fillet012
  Edges = 1 edges r=5: [Edge54]
FEATURE [Part::Fillet] Fillet014  label="Wheel Sensor Mount"
  Base = -> Fillet013
  Edges = 1 edges r=5: [Edge12]
FEATURE [Part::Chamfer] Chamfer008
  Base = -> Fusion104
  Edges = 1 edges r=0.5: [Edge77]
FEATURE [Part::Chamfer] Chamfer009  label="Switch Mount"
  Base = -> Chamfer008
  Edges = 1 edges r=0.5: [Edge6]
FEATURE [Part::MultiFuse] Fusion157  label="Main Body"
  Shapes = -> [Box015,Box016,Box017,Cut045053]
FEATURE [Part::MultiFuse] Fusion158  label="Arduino Mount Holes"
  Shapes = -> [Cylinder115,Cylinder116,Cylinder117,Cylinder118]
FEATURE [Part::MultiFuse] Fusion159  label="Motor Bracket Mount Holes"
  Shapes = -> [Cylinder131,Cylinder130]
FEATURE [Part::Cylinder] Cylinder133  label="Sensor Mount Hole001"
  Angle = 360
  AttacherType = Attacher::AttachEngine3D
  Height = 14
  Placement = pos=(-39,11,-22) rot=(1,0,0;1.5708rad)
  Radius = 1.5
FEATURE [Part::Cylinder] Cylinder134  label="Cylinder221"
  Angle = 360
  AttacherType = Attacher::AttachEngine3D
  Height = 14
  Placement = pos=(-38,11,4) rot=(1,0,0;1.5708rad)
  Radius = 1.5
FEATURE [Part::Cylinder] Cylinder135  label="Cylinder222"
  Angle = 360
  AttacherType = Attacher::AttachEngine3D
  Height = 14
  Placement = pos=(-28,11,4) rot=(1,0,0;1.5708rad)
  Radius = 1.5
FEATURE [Part::MultiFuse] Fusion160  label="Motor Bracket Mount Holes001"
  Shapes = -> [Cylinder135,Cylinder134]
FEATURE [Part::MultiFuse] Fusion161
  Shapes = -> [Cylinder133,Fusion160]
FEATURE [Part::MultiFuse] Fusion162
  Shapes = -> [Fusion159,Cylinder129]
FEATURE [Part::Mirroring] Part__Mirroring014  label="Fusion161 (Mirror #15)"
  Base = (0,0,0)
  Normal = (1,0,0)
  Placement = pos=(27,0,0) rot=(0,0,1;0rad)
  Source = -> Fusion161
FEATURE [Part::Cut] Cut045057
  Base = -> Fusion157
  Tool = -> Part__Mirroring014
FEATURE [Part::Cut] Cut045058
  Base = -> Cut045057
  Tool = -> Fusion162
FEATURE [Part::MultiFuse] Fusion163  label="Nut Holes"
  Shapes = -> [Cut045049,Cut045050,Cut045051,Cut045052]
FEATURE [Part::Cut] Cut045059
  Base = -> Cut045058
  Tool = -> Fusion163
FEATURE [Part::Cut] Cut045060
  Base = -> Cut045059
  Tool = -> Fusion158
FEATURE [Part::Chamfer] Chamfer010
  Base = -> Cut045060
  Edges = 1 edges r=25: [Edge2]
FEATURE [Part::Chamfer] Chamfer011
  Base = -> Chamfer010
  Edges = 1 edges r=25: [Edge258]
FEATURE [Part::Chamfer] Chamfer012
  Base = -> Chamfer011
  Edges = 1 edges r=25: [Edge12]
FEATURE [Part::Chamfer] Chamfer013
  Base = -> Chamfer012
  Edges = 1 edges r=25: [Edge154]
FEATURE [Part::MultiFuse] Fusion164  label="Charging Wire Holes"
  Shapes = -> [Cylinder123,Cylinder124,Part__Mirroring012,Part__Mirroring013]
FEATURE [Part::Cut] Cut045061
  Base = -> Chamfer013
  Tool = -> Fusion164
FEATURE [Part::Chamfer] Chamfer014
  Base = -> Cut045061
  Edges = 1 edges r=2: [Edge12]
FEATURE [Part::Chamfer] Chamfer015
  Base = -> Chamfer014
  Edges = 1 edges r=2: [Edge13]
FEATURE [Part::Chamfer] Chamfer016
  Base = -> Chamfer015
  Edges = 1 edges r=2: [Edge14]
FEATURE [Part::Chamfer] Chamfer017
  Base = -> Chamfer016
  Edges = 1 edges r=2: [Edge94]
FEATURE [Part::Chamfer] Chamfer018
  Base = -> Chamfer017
  Edges = 1 edges r=2: [Edge9]
FEATURE [Part::Chamfer] Chamfer019
  Base = -> Chamfer018
  Edges = 1 edges r=2: [Edge10]
FEATURE [Part::Fuse] Fusion165
  Base = -> Fusion057
  Tool = -> Fusion058
FEATURE [Part::Cut] Cut045062  label="Main Body001"
  Base = -> Chamfer019
  Tool = -> Fusion165
FEATURE [Part::Cylinder] Cylinder136  label="Cylinder223"
  Angle = 360
  AttacherType = Attacher::AttachEngine3D
  Height = 14
  Placement = pos=(-38,11,4) rot=(1,0,0;1.5708rad)
  Radius = 1.5
FEATURE [Part::Cylinder] Cylinder137  label="Cylinder224"
  Angle = 360
  AttacherType = Attacher::AttachEngine3D
  Height = 14
  Placement = pos=(-28,11,4) rot=(1,0,0;1.5708rad)
  Radius = 1.5
FEATURE [Part::Fuse] Fusion166
  Base = -> Box011
  Tool = -> Box014027
FEATURE [Part::Fuse] Fusion167  label="Motor Mount Holes to Main"
  Base = -> Cylinder136
  Tool = -> Cylinder137
FEATURE [Part::Cut] Cut045063
  Base = -> Fusion166
  Tool = -> Fusion167
FEATURE [Part::Cut] Cut045064
  Base = -> Cut045063
  Tool = -> Fusion073
FEATURE [Part::Fillet] Fillet015
  Base = -> Cut045064
  Edges = 1 edges r=5: [Edge35]
FEATURE [Part::Fillet] Fillet016
  Base = -> Fillet015
  Edges = 1 edges r=10: [Edge11]
FEATURE [Part::Fillet] Fillet017
  Base = -> Fillet016
  Edges = 1 edges r=1: [Edge6]
FEATURE [Part::Fillet] Fillet018  label="Motor Mount"
  Base = -> Fillet017
  Edges = 1 edges r=1: [Edge6]
FEATURE [Part::Chamfer] Chamfer020
  Base = -> Cut045019
  Edges = 19 edges r=0.75: [Edge111,Edge114,Edge125,Edge129,Edge135,Edge138,Edge152,Edge155,Edge159,Edge165,Edge168,Edge171,Edge175,Edge181,Edge184,Edge187,Edge191,Edge229,Edge232]
FEATURE [Part::Chamfer] Chamfer021
  Base = -> Chamfer020
  Edges = 17 edges r=0.75: [Edge94,Edge96,Edge98,Edge100,Edge102,Edge104,Edge105,Edge107,Edge112,Edge114,Edge117,Edge119,Edge120,Edge122,Edge124,Edge126,Edge147]
FEATURE [Part::Chamfer] Chamfer022  label="Chamfer Wheel"
  Base = -> Chamfer021
  Edges = 36 edges r=0.75: [Edge373,Edge375,Edge376,Edge377,Edge378,Edge379,Edge380,Edge381,Edge382,Edge383,Edge384,Edge385,Edge386,Edge387,Edge388,Edge389,Edge390,Edge391,Edge392,Edge393,Edge394,Edge395,Edge396,Edge397,Edge398,Edge399,Edge400,Edge401,Edge402,Edge403,Edge404,Edge405,Edge406,Edge407,Edge408,Edge409]
